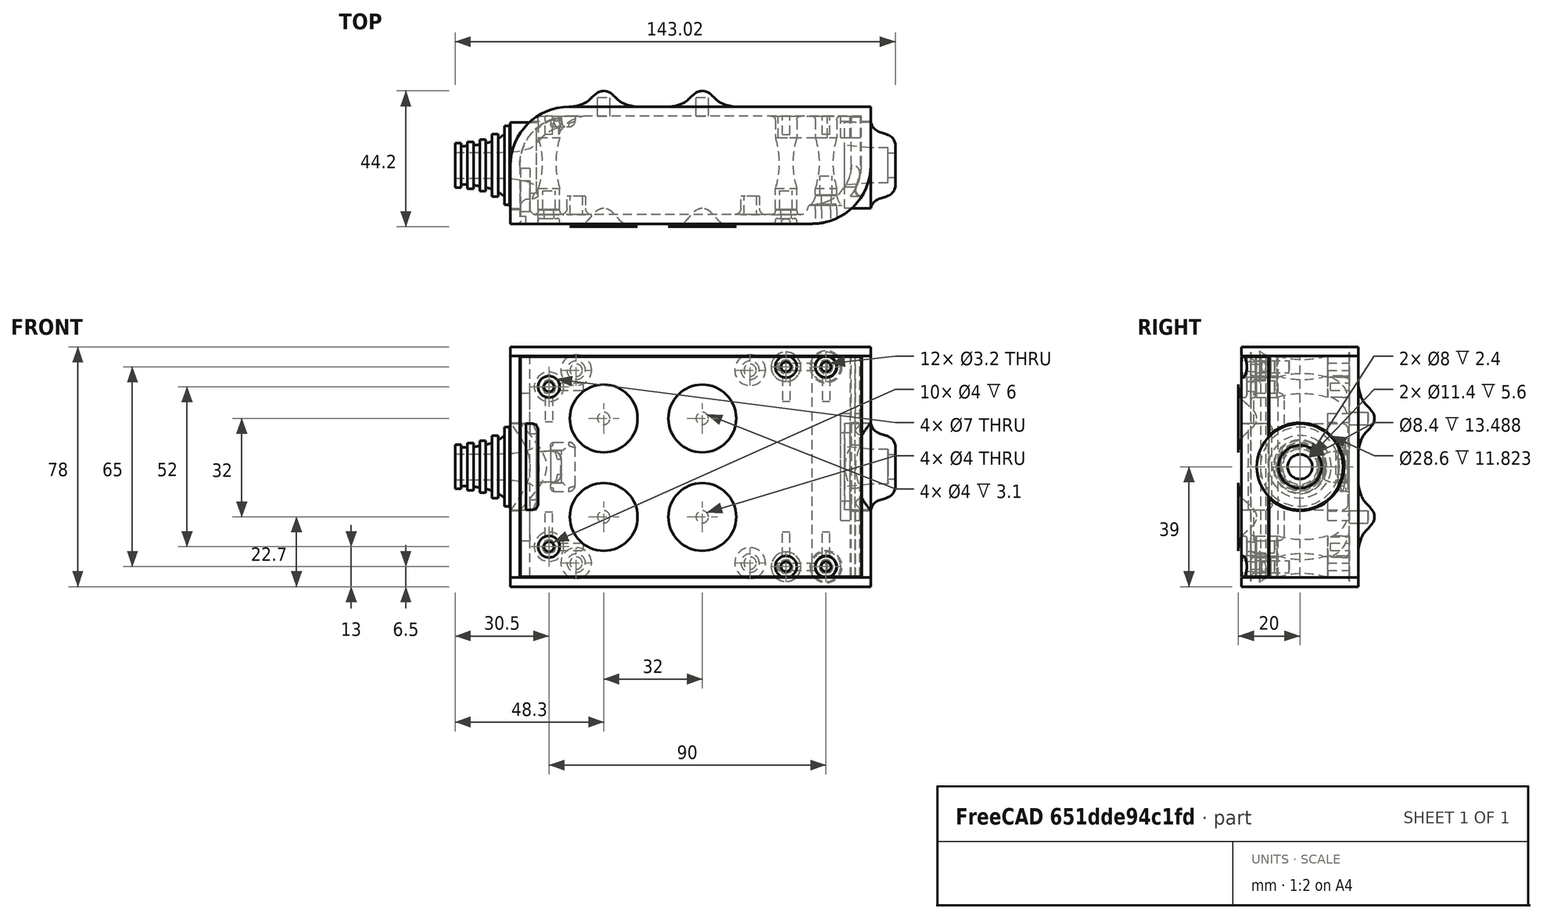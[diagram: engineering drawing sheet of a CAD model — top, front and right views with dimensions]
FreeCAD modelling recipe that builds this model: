
FCSTD DOCUMENT  (FreeCAD 0.19R0.19.2)
Label: enclosure_093
License: All rights reserved
LicenseURL: http://en.wikipedia.org/wiki/All_rights_reserved
objects: Part::Feature×72, Part::Revolution×72, Part::MultiFuse×52, Sketcher::SketchObject×29, Part::Fillet×22, Part::Cylinder×22, Part::Cut×19, Part::Extrusion×18, Part::Box×12, App::MeasureDistance×3
note: 318 computed .brp shape members not serialized (recipe doc carries the construction recipe); baked Part::Feature solids carry a one-line shape summary decoded from their .brp

FEATURE [Sketcher::SketchObject] Sketch  label="topSketch"
  FullyConstrained = true
  sketch-geometry (13):
    g0: LineSegment StartX=117 StartY=19 StartZ=0 EndX=117 EndY=38 EndZ=0
    g1: ArcOfCircle CenterX=98 CenterY=19 CenterZ=0 NormalX=0 NormalY=0 NormalZ=1 AngleXU=0 Radius=19 StartAngle=5.7297 EndAngle=6.28319
    g2: LineSegment StartX=0 StartY=3 StartZ=0 EndX=0 EndY=19 EndZ=0
    g3: LineSegment StartX=19 StartY=38 StartZ=0 EndX=117 EndY=38 EndZ=0
    g4: ArcOfCircle CenterX=19 CenterY=19 CenterZ=0 NormalX=0 NormalY=0 NormalZ=1 AngleXU=0 Radius=19 StartAngle=1.5708 EndAngle=3.14159
    g5: ArcOfCircle CenterX=19 CenterY=19 CenterZ=0 NormalX=0 NormalY=0 NormalZ=1 AngleXU=0 Radius=16 StartAngle=1.5708 EndAngle=3.14159
    g6: ArcOfCircle CenterX=98 CenterY=19 CenterZ=0 NormalX=0 NormalY=0 NormalZ=1 AngleXU=0 Radius=16 StartAngle=5.60905 EndAngle=6.28319
    g7: LineSegment StartX=114 StartY=19 StartZ=0 EndX=114 EndY=35 EndZ=0
    g8: LineSegment StartX=110.5 StartY=9.01251 StartZ=0 EndX=114.163 EndY=9.01251 EndZ=0
    g9: LineSegment StartX=114 StartY=35 StartZ=0 EndX=19 EndY=35 EndZ=0
    g10: LineSegment StartX=0 StartY=3 StartZ=0 EndX=0 EndY=0 EndZ=0
    g11: LineSegment StartX=3 StartY=0 StartZ=0 EndX=0 EndY=0 EndZ=0
    g12: LineSegment StartX=3 StartY=19 StartZ=0 EndX=3 EndY=0 EndZ=0
  constraints (33):
    c: Vertical(g0)
    c: Distance(g0) = 19
    c: Block(g0)
    c: Coincident(g1,g0)
    c: Block(g1)
    c: Vertical(g2)
    c: Block(g2)
    c: Coincident(g3,g0)
    c: Horizontal(g3)
    c: Distance(g3) = 98
    c: Coincident(g4,g3)
    c: Coincident(g4,g2)
    c: Block(g4)
    c: Coincident(g5,g4)
    c: Coincident(g6,g1)
    c: Block(g6)
    c: Block(g5)
    c: Coincident(g7,g6)
    c: Vertical(g7)
    c: Coincident(g8,g6)
    c: Coincident(g8,g1)
    c: Coincident(g9,g7)
    c: Coincident(g9,g5)
    c: Horizontal(g9)
    c: Tangent(g9,g5)
    c: Coincident(g10,g2)
    c: Distance(g10) = 3
    c: Vertical(g10)
    c: Coincident(g11,g10)
    c: Horizontal(g11)
    c: Coincident(g12,g5)
    c: Coincident(g12,g11)
    c: Vertical(g12)
FEATURE [Sketcher::SketchObject] Sketch001  label="bottomSketch"
  FullyConstrained = true
  sketch-geometry (32):
    g0: LineSegment StartX=3.3 StartY=-6.03275e-07 StartZ=0 EndX=98 EndY=-6.03275e-07 EndZ=0
    g1: ArcOfCircle CenterX=98 CenterY=19 CenterZ=0 NormalX=0 NormalY=0 NormalZ=1 AngleXU=0 Radius=19 StartAngle=4.71239 EndAngle=5.71103
    g2: LineSegment StartX=6.3 StartY=8 StartZ=0 EndX=3.3 EndY=8 EndZ=0
    g3: LineSegment StartX=3.3 StartY=8 StartZ=0 EndX=3.3 EndY=-6.03275e-07 EndZ=0
    g4: ArcOfCircle CenterX=8.3 CenterY=5 CenterZ=0 NormalX=0 NormalY=0 NormalZ=1 AngleXU=0 Radius=2 StartAngle=3.14159 EndAngle=4.71239
    g5: LineSegment StartX=6.3 StartY=8 StartZ=0 EndX=6.3 EndY=5 EndZ=0
    g6: ArcOfCircle CenterX=98 CenterY=19 CenterZ=0 NormalX=0 NormalY=0 NormalZ=1 AngleXU=0 Radius=12.7 StartAngle=4.71239 EndAngle=6.28319
    g7: LineSegment StartX=94.7 StartY=3 StartZ=0 EndX=8.3 EndY=3 EndZ=0
    g8-g12: Circle x5 (B-spline internal-alignment scaffolding for g13; pole/knot coordinates omitted)
    g13: BSplineCurve PolesCount=5 KnotsCount=3 Degree=3 IsPeriodic=0
    g14: GeomPoint X=98 Y=6.3 Z=0
    g15: GeomPoint X=96.3938 Y=4.71946 Z=0
    g16: GeomPoint X=94.7 Y=3 Z=0
    g17-g23: Circle x7 (B-spline internal-alignment scaffolding for g24; pole/knot coordinates omitted)
    g24: BSplineCurve PolesCount=7 KnotsCount=5 Degree=3 IsPeriodic=0
    g25-g29: GeomPoint x5 (B-spline internal-alignment scaffolding for g24; pole/knot coordinates omitted)
    g30: ArcOfCircle CenterX=98 CenterY=19 CenterZ=0 NormalX=0 NormalY=0 NormalZ=1 AngleXU=0 Radius=15.7 StartAngle=5.81226 EndAngle=6.28319
    g31: LineSegment StartX=110.7 StartY=19 StartZ=0 EndX=113.7 EndY=19 EndZ=0
  constraints (41):
    c: Horizontal(g0)
    c: Coincident(g1,g0)
    c: Block(g1)
    c: Horizontal(g2)
    c: Distance(g2) = 3
    c: Coincident(g3,g2)
    c: Vertical(g3)
    c: Coincident(g3,g0)
    c: Block(g4)
    c: Block(g2)
    c: Coincident(g5,g2)
    c: Coincident(g5,g4)
    c: Vertical(g5)
    c: Coincident(g6,g1)
    c: Block(g6)
    c: Coincident(g7,g4)
    c: Horizontal(g7)
    c: Block(g0)
    c: Block(g7)
    c: Block(g3)
    c: Coincident(g13,g6)
    c: Weight(g8) = 1
    c: Equal(g8, g9-g12) x4
    c: Coincident(g13,g7)
    c: InternalAlignment(g8-g12 -> g13) x5
    c: InternalAlignment(g14,g13)
    c: InternalAlignment(g15,g13)
    c: InternalAlignment(g16,g13)
    c: Block(g13)
    c: Weight(g17) = 1
    c: Equal(g17, g18-g23) x6
    c: Coincident(g24,g1)
    c: InternalAlignment(g17-g23 -> g24) x7
    c: InternalAlignment(g25-g29 -> g24) x5
    c: Block(g24)
    c: Coincident(g30,g24)
    c: Coincident(g31,g6)
    c: Coincident(g31,g30)
    c: Horizontal(g31)
    c: Block(g31)
    c: Block(g30)
FEATURE [Part::Extrusion] Extrude  label="top"
  Base = -> Sketch
  Dir = (0,0,1)
  DirMode = 2
  FaceMakerClass = Part::FaceMakerBullseye
  LengthFwd = 72
  LengthRev = 0
  Solid = true
  Symmetric = false
FEATURE [Part::Extrusion] Extrude001  label="bottom"
  Base = -> Sketch001
  Dir = (0,0,1)
  DirMode = 2
  FaceMakerClass = Part::FaceMakerBullseye
  LengthFwd = 71.4
  LengthRev = 0
  Placement = pos=(0,0,0.3) rot=(0,0,1;0rad)
  Solid = true
  Symmetric = false
FEATURE [Sketcher::SketchObject] Sketch002  label="topSketch001"
  FullyConstrained = true
  sketch-geometry (6):
    g0: LineSegment StartX=19 StartY=38 StartZ=0 EndX=117 EndY=38 EndZ=0
    g1: ArcOfCircle CenterX=19 CenterY=19 CenterZ=0 NormalX=0 NormalY=0 NormalZ=1 AngleXU=0 Radius=19 StartAngle=1.5708 EndAngle=3.14159
    g2: LineSegment StartX=117 StartY=38 StartZ=0 EndX=117 EndY=19 EndZ=0
    g3: LineSegment StartX=98 StartY=1.0161e-12 StartZ=0 EndX=5.22862e-06 EndY=1.0161e-12 EndZ=0
    g4: LineSegment StartX=5.22862e-06 StartY=19 StartZ=0 EndX=5.22862e-06 EndY=1.0161e-12 EndZ=0
    g5: ArcOfCircle CenterX=98 CenterY=19 CenterZ=0 NormalX=0 NormalY=0 NormalZ=1 AngleXU=0 Radius=19 StartAngle=4.71239 EndAngle=6.28319
  constraints (16):
    c: Horizontal(g0)
    c: Distance(g0) = 98
    c: Coincident(g1,g0)
    c: Block(g1)
    c: Coincident(g2,g0)
    c: Vertical(g2)
    c: Distance(g2) = 19
    c: Horizontal(g3)
    c: Coincident(g4,g1)
    c: Vertical(g4)
    c: Coincident(g3,g4)
    c: Block(g3)
    c: Coincident(g5,g2)
    c: Coincident(g5,g3)
    c: Block(g0)
    c: Block(g5)
FEATURE [Part::Extrusion] Extrude002  label="sideA"
  Base = -> Sketch002
  Dir = (0,0,1)
  DirMode = 2
  FaceMakerClass = Part::FaceMakerBullseye
  LengthFwd = 3
  LengthRev = 0
  Placement = pos=(0,0,-3) rot=(0,0,1;0rad)
  Solid = true
  Symmetric = false
FEATURE [Sketcher::SketchObject] Sketch003  label="topSketch002"
  FullyConstrained = true
  sketch-geometry (6):
    g0: LineSegment StartX=19 StartY=38 StartZ=0 EndX=117 EndY=38 EndZ=0
    g1: ArcOfCircle CenterX=19 CenterY=19 CenterZ=0 NormalX=0 NormalY=0 NormalZ=1 AngleXU=0 Radius=19 StartAngle=1.5708 EndAngle=3.14159
    g2: LineSegment StartX=117 StartY=38 StartZ=0 EndX=117 EndY=19 EndZ=0
    g3: LineSegment StartX=98 StartY=1.0161e-12 StartZ=0 EndX=5.22862e-06 EndY=1.0161e-12 EndZ=0
    g4: LineSegment StartX=5.22862e-06 StartY=19 StartZ=0 EndX=5.22862e-06 EndY=1.0161e-12 EndZ=0
    g5: ArcOfCircle CenterX=98 CenterY=19 CenterZ=0 NormalX=0 NormalY=0 NormalZ=1 AngleXU=0 Radius=19 StartAngle=4.71239 EndAngle=6.28319
  constraints (16):
    c: Horizontal(g0)
    c: Distance(g0) = 98
    c: Coincident(g1,g0)
    c: Block(g1)
    c: Coincident(g2,g0)
    c: Vertical(g2)
    c: Distance(g2) = 19
    c: Horizontal(g3)
    c: Coincident(g4,g1)
    c: Vertical(g4)
    c: Coincident(g3,g4)
    c: Block(g3)
    c: Coincident(g5,g2)
    c: Coincident(g5,g3)
    c: Block(g0)
    c: Block(g5)
FEATURE [Part::Extrusion] Extrude003  label="sideB"
  Base = -> Sketch003
  Dir = (0,0,1)
  DirMode = 2
  FaceMakerClass = Part::FaceMakerBullseye
  LengthFwd = 3
  LengthRev = 0
  Placement = pos=(0,0,72) rot=(0,0,1;0rad)
  Solid = true
  Symmetric = false
FEATURE [Sketcher::SketchObject] Sketch004
  FullyConstrained = true
  MapMode = 3
  Placement = pos=(0,0,0) rot=(1,0,0;1.5708rad)
  Support = -> [Extrude]
  sketch-geometry (8):
    g0: Circle CenterX=80.351 CenterY=-67.6202 CenterZ=0 NormalX=0 NormalY=0 NormalZ=1 AngleXU=0 Radius=2
    g1: Circle CenterX=80.351 CenterY=-67.6202 CenterZ=0 NormalX=0 NormalY=0 NormalZ=1 AngleXU=0 Radius=3
    g2: Circle CenterX=80.351 CenterY=-4.92017 CenterZ=0 NormalX=0 NormalY=0 NormalZ=1 AngleXU=0 Radius=2
    g3: Circle CenterX=80.351 CenterY=-4.92017 CenterZ=0 NormalX=0 NormalY=0 NormalZ=1 AngleXU=0 Radius=3
    g4: Circle CenterX=23.851 CenterY=-4.92017 CenterZ=0 NormalX=0 NormalY=0 NormalZ=1 AngleXU=0 Radius=2
    g5: Circle CenterX=23.851 CenterY=-4.92017 CenterZ=0 NormalX=0 NormalY=0 NormalZ=1 AngleXU=0 Radius=3
    g6: Circle CenterX=23.851 CenterY=-67.6202 CenterZ=0 NormalX=0 NormalY=0 NormalZ=1 AngleXU=0 Radius=2
    g7: Circle CenterX=23.851 CenterY=-67.6202 CenterZ=0 NormalX=0 NormalY=0 NormalZ=1 AngleXU=0 Radius=3
  constraints (8):
    c: Block(g3)
    c: Block(g2)
    c: Block(g1)
    c: Block(g0)
    c: Block(g6)
    c: Block(g7)
    c: Block(g4)
    c: Block(g5)
FEATURE [Part::Extrusion] Extrude004
  Base = -> Sketch004
  Dir = (0,-1,2e-16)
  DirMode = 2
  FaceMakerClass = Part::FaceMakerBullseye
  LengthFwd = 6
  LengthRev = 0
  Placement = pos=(0,9,0) rot=(0,0,1;0rad)
  Solid = true
  Symmetric = false
FEATURE [Sketcher::SketchObject] Sketch005
  FullyConstrained = true
  MapMode = 3
  Placement = pos=(0,0,0) rot=(1,0,0;1.5708rad)
  Support = -> [Extrude]
  sketch-geometry (8):
    g0: Circle CenterX=80.351 CenterY=-67.6202 CenterZ=0 NormalX=0 NormalY=0 NormalZ=1 AngleXU=0 Radius=3
    g1: Circle CenterX=80.351 CenterY=-4.92017 CenterZ=0 NormalX=0 NormalY=0 NormalZ=1 AngleXU=0 Radius=3
    g2: Circle CenterX=23.851 CenterY=-4.92017 CenterZ=0 NormalX=0 NormalY=0 NormalZ=1 AngleXU=0 Radius=3
    g3: Circle CenterX=23.851 CenterY=-67.6202 CenterZ=0 NormalX=0 NormalY=0 NormalZ=1 AngleXU=0 Radius=3
    g4: Circle CenterX=23.851 CenterY=-67.6202 CenterZ=0 NormalX=0 NormalY=0 NormalZ=1 AngleXU=0 Radius=5
    g5: Circle CenterX=80.351 CenterY=-67.6202 CenterZ=0 NormalX=0 NormalY=0 NormalZ=1 AngleXU=0 Radius=5
    g6: Circle CenterX=23.851 CenterY=-4.92017 CenterZ=0 NormalX=0 NormalY=0 NormalZ=1 AngleXU=0 Radius=5
    g7: Circle CenterX=80.351 CenterY=-4.92017 CenterZ=0 NormalX=0 NormalY=0 NormalZ=1 AngleXU=0 Radius=5
  constraints (8):
    c: Block(g1)
    c: Block(g0)
    c: Block(g3)
    c: Block(g2)
    c: Block(g5)
    c: Block(g4)
    c: Block(g6)
    c: Block(g7)
FEATURE [Part::Extrusion] Extrude005
  Base = -> Sketch005
  Dir = (0,-1,2e-16)
  DirMode = 2
  FaceMakerClass = Part::FaceMakerBullseye
  LengthFwd = 2
  LengthRev = 0
  Solid = true
  Symmetric = false
FEATURE [Sketcher::SketchObject] Sketch006
  FullyConstrained = true
  MapMode = 3
  Placement = pos=(0,0,0) rot=(1,0,0;1.5708rad)
  sketch-geometry (8):
    g0: Circle CenterX=80.351 CenterY=-67.6202 CenterZ=0 NormalX=0 NormalY=0 NormalZ=1 AngleXU=0 Radius=3
    g1: Circle CenterX=80.351 CenterY=-4.92017 CenterZ=0 NormalX=0 NormalY=0 NormalZ=1 AngleXU=0 Radius=3
    g2: Circle CenterX=23.851 CenterY=-4.92017 CenterZ=0 NormalX=0 NormalY=0 NormalZ=1 AngleXU=0 Radius=3
    g3: Circle CenterX=23.851 CenterY=-67.6202 CenterZ=0 NormalX=0 NormalY=0 NormalZ=1 AngleXU=0 Radius=3
    g4: Circle CenterX=23.851 CenterY=-67.6202 CenterZ=0 NormalX=0 NormalY=0 NormalZ=1 AngleXU=0 Radius=5
    g5: Circle CenterX=80.351 CenterY=-67.6202 CenterZ=0 NormalX=0 NormalY=0 NormalZ=1 AngleXU=0 Radius=5
    g6: Circle CenterX=23.851 CenterY=-4.92017 CenterZ=0 NormalX=0 NormalY=0 NormalZ=1 AngleXU=0 Radius=5
    g7: Circle CenterX=80.351 CenterY=-4.92017 CenterZ=0 NormalX=0 NormalY=0 NormalZ=1 AngleXU=0 Radius=5
  constraints (8):
    c: Block(g1)
    c: Block(g0)
    c: Block(g3)
    c: Block(g2)
    c: Block(g5)
    c: Block(g4)
    c: Block(g6)
    c: Block(g7)
FEATURE [Part::Extrusion] Extrude007
  Base = -> Sketch006
  Dir = (0,-1,2e-16)
  DirMode = 2
  FaceMakerClass = Part::FaceMakerBullseye
  LengthFwd = 2
  LengthRev = 0
  Solid = true
  Symmetric = false
FEATURE [Part::Fillet] Fillet
  Base = -> Extrude007
  Edges = 4 edges r=1.99: [Edge6,Edge12,Edge18,Edge24]
FEATURE [Part::Cut] Cut
  Base = -> Extrude005
  Placement = pos=(0,5,0) rot=(0,0,1;0rad)
  Tool = -> Fillet
FEATURE [Part::MultiFuse] Fusion  label="pCBScrews"
  Placement = pos=(-2.5,0,72.3) rot=(0,0,1;0rad)
  Shapes = -> [Extrude004,Cut]
FEATURE [App::MeasureDistance] Distance  label="Distance: 0.69 mm"
  Distance = 0.685967
  P1 = (24.0138,2.9647,0.3)
  P2 = (23.8901,3,-0.373787)
FEATURE [App::MeasureDistance] Distance001  label="Distance: 0.53 mm"
  Distance = 0.533607
  P1 = (80.2939,3,72.2334)
  P2 = (80.281,2.99661,71.7)
FEATURE [Part::Fillet] Fillet001
  Base = -> Extrude001
  Edges = 1 edges r=2.4: [Edge17]
FEATURE [Part::Fillet] Fillet002  label="bottom001"
  Base = -> Fillet001
  Edges = 1 edges r=2.4: [Edge36]
FEATURE [Part::Fillet] Fillet003  label="top001"
  Base = -> Extrude
  Edges = 1 edges r=2: [Edge1]
FEATURE [Sketcher::SketchObject] Sketch007
  FullyConstrained = true
  sketch-geometry (16):
    g0: LineSegment StartX=4 StartY=0 StartZ=0 EndX=4 EndY=2.4 EndZ=0
    g1: LineSegment StartX=4 StartY=2.4 StartZ=0 EndX=7 EndY=2.4 EndZ=0
    g2: LineSegment StartX=4 StartY=0 StartZ=0 EndX=5.7 EndY=0 EndZ=0
    g3: LineSegment StartX=5.7 StartY=0 StartZ=0 EndX=5.7 EndY=-5.6 EndZ=0
    g4-g8: Circle x5 (B-spline internal-alignment scaffolding for g9; pole/knot coordinates omitted)
    g9: BSplineCurve PolesCount=5 KnotsCount=3 Degree=3 IsPeriodic=0
    g10: GeomPoint X=7 Y=2.4 Z=0
    g11: GeomPoint X=10.4582 Y=-1.55472 Z=0
    g12: GeomPoint X=14 Y=-5.6 Z=0
    g13: LineSegment StartX=14 StartY=-5.6 StartZ=0 EndX=14 EndY=-14.1 EndZ=0
    g14: LineSegment StartX=14 StartY=-14.1 StartZ=0 EndX=6.5 EndY=-14.1 EndZ=0
    g15: LineSegment StartX=5.7 StartY=-5.6 StartZ=0 EndX=6.5 EndY=-14.1 EndZ=0
  constraints (28):
    c: Distance(g0) = 2.4
    c: Vertical(g0)
    c: Block(g0)
    c: Coincident(g1,g0)
    c: Horizontal(g1)
    c: Distance(g1) = 3
    c: Coincident(g2,g0)
    c: Horizontal(g2)
    c: Distance(g2) = 1.7
    c: Coincident(g3,g2)
    c: Vertical(g3)
    c: Distance(g3) = 5.6
    c: Coincident(g9,g1)
    c: Weight(g4) = 1
    c: Equal(g4, g5-g8) x4
    c: InternalAlignment(g4-g8 -> g9) x5
    c: InternalAlignment(g10,g9)
    c: InternalAlignment(g11,g9)
    c: InternalAlignment(g12,g9)
    c: Block(g9)
    c: Coincident(g13,g9)
    c: Vertical(g13)
    c: Distance(g13) = 8.5
    c: Coincident(g14,g13)
    c: Horizontal(g14)
    c: Distance(g14) = 7.5
    c: Coincident(g15,g3)
    c: Coincident(g15,g14)
FEATURE [Part::Feature] Face
  shape: bbox 10 x 16.5 x 2e-07 mm, 1 faces, 0 solids (baked)
FEATURE [Part::Revolution] Revolve  label="plugHousing"
  Angle = 360
  Axis = (0,1,0)
  Base = (0,0,0)
  FaceMakerClass = Part::FaceMakerBullseye
  Placement = pos=(0,0,36.15) rot=(0,0,1;0rad)
  Solid = false
  Source = -> Face
  Symmetric = false
FEATURE [Part::Feature] Face001
  shape: bbox 10 x 16.5 x 2e-07 mm, 1 faces, 0 solids (baked)
FEATURE [Part::Revolution] Revolve001  label="plugHousing001"
  Angle = 360
  Axis = (0,1,0)
  Base = (0,0,0)
  FaceMakerClass = Part::FaceMakerBullseye
  Placement = pos=(0,0,36.15) rot=(0,0,1;0rad)
  Solid = false
  Source = -> Face001
  Symmetric = false
FEATURE [Part::MultiFuse] Fusion001  label="plugHousing002"
  Placement = pos=(0,0,0) rot=(0,0,1;1.5708rad)
  Shapes = -> [Revolve001,Revolve]
FEATURE [Part::Feature] Face002
  shape: bbox 10 x 16.5 x 2e-07 mm, 1 faces, 0 solids (baked)
FEATURE [Part::Revolution] Revolve003  label="plugHousing005"
  Angle = 360
  Axis = (0,1,0)
  Base = (0,0,0)
  FaceMakerClass = Part::FaceMakerBullseye
  Placement = pos=(0,0,36.15) rot=(0,0,1;0rad)
  Solid = false
  Source = -> Face002
  Symmetric = false
FEATURE [Part::Feature] Face003
  shape: bbox 10 x 16.5 x 2e-07 mm, 1 faces, 0 solids (baked)
FEATURE [Part::Revolution] Revolve002  label="plugHousing003"
  Angle = 360
  Axis = (0,1,0)
  Base = (0,0,0)
  FaceMakerClass = Part::FaceMakerBullseye
  Placement = pos=(0,0,36.15) rot=(0,0,1;0rad)
  Solid = false
  Source = -> Face003
  Symmetric = false
FEATURE [Part::MultiFuse] Fusion002  label="plugHousing004"
  Placement = pos=(0,0,0) rot=(0,0,1;1.5708rad)
  Shapes = -> [Revolve002,Revolve003]
FEATURE [Part::MultiFuse] Fusion003  label="plugHousing006"
  Placement = pos=(0,19,0) rot=(0,0,1;3.14159rad)
  Shapes = -> [Fusion002,Fusion001]
FEATURE [Part::Feature] Face004
  shape: bbox 10 x 16.5 x 2e-07 mm, 1 faces, 0 solids (baked)
FEATURE [Part::Revolution] Revolve006  label="plugHousing010"
  Angle = 360
  Axis = (0,1,0)
  Base = (0,0,0)
  FaceMakerClass = Part::FaceMakerBullseye
  Placement = pos=(0,0,36.15) rot=(0,0,1;0rad)
  Solid = false
  Source = -> Face004
  Symmetric = false
FEATURE [Part::Feature] Face005
  shape: bbox 10 x 16.5 x 2e-07 mm, 1 faces, 0 solids (baked)
FEATURE [Part::Revolution] Revolve007  label="plugHousing011"
  Angle = 360
  Axis = (0,1,0)
  Base = (0,0,0)
  FaceMakerClass = Part::FaceMakerBullseye
  Placement = pos=(0,0,36.15) rot=(0,0,1;0rad)
  Solid = false
  Source = -> Face005
  Symmetric = false
FEATURE [Part::Feature] Face006
  shape: bbox 10 x 16.5 x 2e-07 mm, 1 faces, 0 solids (baked)
FEATURE [Part::Revolution] Revolve004  label="plugHousing007"
  Angle = 360
  Axis = (0,1,0)
  Base = (0,0,0)
  FaceMakerClass = Part::FaceMakerBullseye
  Placement = pos=(0,0,36.15) rot=(0,0,1;0rad)
  Solid = false
  Source = -> Face006
  Symmetric = false
FEATURE [Part::MultiFuse] Fusion004  label="plugHousing009"
  Placement = pos=(0,0,0) rot=(0,0,1;1.5708rad)
  Shapes = -> [Revolve004,Revolve007]
FEATURE [Part::Feature] Face007
  shape: bbox 10 x 16.5 x 2e-07 mm, 1 faces, 0 solids (baked)
FEATURE [Part::Revolution] Revolve005  label="plugHousing008"
  Angle = 360
  Axis = (0,1,0)
  Base = (0,0,0)
  FaceMakerClass = Part::FaceMakerBullseye
  Placement = pos=(0,0,36.15) rot=(0,0,1;0rad)
  Solid = false
  Source = -> Face007
  Symmetric = false
FEATURE [Part::MultiFuse] Fusion005  label="plugHousing012"
  Placement = pos=(0,0,0) rot=(0,0,1;1.5708rad)
  Shapes = -> [Revolve006,Revolve005]
FEATURE [Part::MultiFuse] Fusion006  label="plugHousing013"
  Placement = pos=(0,19,0) rot=(0,0,1;3.14159rad)
  Shapes = -> [Fusion005,Fusion004]
FEATURE [Part::MultiFuse] Fusion007  label="plugHousing014"
  Placement = pos=(122.621,0,-0.15) rot=(0,0,1;0rad)
  Shapes = -> [Fusion003,Fusion006]
FEATURE [Part::Cylinder] Cylinder002
  Angle = 360
  AttacherType = Attacher::AttachEngine3D
  Height = 20
  Placement = pos=(0,0,36.15) rot=(0,0,1;0rad)
  Radius = 4
FEATURE [Part::Cylinder] Cylinder003
  Angle = 360
  AttacherType = Attacher::AttachEngine3D
  Height = 10
  Placement = pos=(0,0,36.15) rot=(0,0,1;0rad)
  Radius = 4
FEATURE [Part::MultiFuse] Fusion009  label="removeToCreateHoleForPlugHousing"
  Placement = pos=(70,19,36.15) rot=(0,1,0;1.5708rad)
  Shapes = -> [Cylinder002,Cylinder003]
FEATURE [Part::Cylinder] Cylinder004
  Angle = 360
  AttacherType = Attacher::AttachEngine3D
  Height = 20
  Placement = pos=(0,0,36.15) rot=(0,0,1;0rad)
  Radius = 4
FEATURE [Part::Cylinder] Cylinder005
  Angle = 360
  AttacherType = Attacher::AttachEngine3D
  Height = 10
  Placement = pos=(0,0,36.15) rot=(0,0,1;0rad)
  Radius = 4
FEATURE [Part::MultiFuse] Fusion010  label="removeToCreateHoleForPlugHousing001"
  Placement = pos=(70,19,36.15) rot=(0,1,0;1.5708rad)
  Shapes = -> [Cylinder004,Cylinder005]
FEATURE [Part::Cut] Cut001
  Base = -> Fillet003
  Tool = -> Fusion010
FEATURE [Part::Cut] Cut002  label="Bottom"
  Base = -> Fillet002
  Tool = -> Fusion009
FEATURE [Part::Feature] Face008
  shape: bbox 10 x 16.5 x 2e-07 mm, 1 faces, 0 solids (baked)
FEATURE [Part::Revolution] Revolve011  label="plugHousing021"
  Angle = 360
  Axis = (0,1,0)
  Base = (0,0,0)
  FaceMakerClass = Part::FaceMakerBullseye
  Placement = pos=(0,0,36.15) rot=(0,0,1;0rad)
  Solid = false
  Source = -> Face008
  Symmetric = false
FEATURE [Part::Feature] Face009
  shape: bbox 10 x 16.5 x 2e-07 mm, 1 faces, 0 solids (baked)
FEATURE [Part::Revolution] Revolve012  label="plugHousing022"
  Angle = 360
  Axis = (0,1,0)
  Base = (0,0,0)
  FaceMakerClass = Part::FaceMakerBullseye
  Placement = pos=(0,0,36.15) rot=(0,0,1;0rad)
  Solid = false
  Source = -> Face009
  Symmetric = false
FEATURE [Part::Feature] Face010 .. Face013  x4 (patterned run collapsed; names and placements below)
  shape: bbox 10 x 16.5 x 2e-07 mm, 1 faces, 0 solids (baked)
FEATURE [Part::Revolution] Revolve015  label="plugHousing027"
  Angle = 360
  Axis = (0,1,0)
  Base = (0,0,0)
  FaceMakerClass = Part::FaceMakerBullseye
  Placement = pos=(0,0,36.15) rot=(0,0,1;0rad)
  Solid = false
  Source = -> Face013
  Symmetric = false
FEATURE [Part::Feature] Face014
  shape: bbox 10 x 16.5 x 2e-07 mm, 1 faces, 0 solids (baked)
FEATURE [Part::Feature] Face015
  shape: bbox 10 x 16.5 x 2e-07 mm, 1 faces, 0 solids (baked)
FEATURE [Part::Feature] Face016
  shape: bbox 10 x 16.5 x 2e-07 mm, 1 faces, 0 solids (baked)
FEATURE [Part::Revolution] Revolve019  label="plugHousing033"
  Angle = 360
  Axis = (0,1,0)
  Base = (0,0,0)
  FaceMakerClass = Part::FaceMakerBullseye
  Placement = pos=(0,0,36.15) rot=(0,0,1;0rad)
  Solid = false
  Source = -> Face016
  Symmetric = false
FEATURE [Part::Feature] Face017
  shape: bbox 10 x 16.5 x 2e-07 mm, 1 faces, 0 solids (baked)
FEATURE [Part::Revolution] Revolve020  label="plugHousing034"
  Angle = 360
  Axis = (0,1,0)
  Base = (0,0,0)
  FaceMakerClass = Part::FaceMakerBullseye
  Placement = pos=(0,0,36.15) rot=(0,0,1;0rad)
  Solid = false
  Source = -> Face017
  Symmetric = false
FEATURE [Part::Feature] Face018
  shape: bbox 10 x 16.5 x 2e-07 mm, 1 faces, 0 solids (baked)
FEATURE [Part::Revolution] Revolve016  label="plugHousing030"
  Angle = 360
  Axis = (0,1,0)
  Base = (0,0,0)
  FaceMakerClass = Part::FaceMakerBullseye
  Placement = pos=(0,0,36.15) rot=(0,0,1;0rad)
  Solid = false
  Source = -> Face018
  Symmetric = false
FEATURE [Part::MultiFuse] Fusion020  label="plugHousing038"
  Placement = pos=(0,0,0) rot=(0,0,1;1.5708rad)
  Shapes = -> [Revolve016,Revolve020]
FEATURE [Part::Feature] Face019
  shape: bbox 10 x 16.5 x 2e-07 mm, 1 faces, 0 solids (baked)
FEATURE [Part::Feature] Face020
  shape: bbox 10 x 16.5 x 2e-07 mm, 1 faces, 0 solids (baked)
FEATURE [Part::Revolution] Revolve017  label="plugHousing031"
  Angle = 360
  Axis = (0,1,0)
  Base = (0,0,0)
  FaceMakerClass = Part::FaceMakerBullseye
  Placement = pos=(0,0,36.15) rot=(0,0,1;0rad)
  Solid = false
  Source = -> Face020
  Symmetric = false
FEATURE [Part::MultiFuse] Fusion021  label="plugHousing039"
  Placement = pos=(0,0,0) rot=(0,0,1;1.5708rad)
  Shapes = -> [Revolve019,Revolve017]
FEATURE [Part::MultiFuse] Fusion023  label="plugHousing041"
  Placement = pos=(0,19,0) rot=(0,0,1;3.14159rad)
  Shapes = -> [Fusion021,Fusion020]
FEATURE [Part::Revolution] Revolve022  label="plugHousing043"
  Angle = 360
  Axis = (0,1,0)
  Base = (0,0,0)
  FaceMakerClass = Part::FaceMakerBullseye
  Placement = pos=(0,0,36.15) rot=(0,0,1;0rad)
  Solid = false
  Source = -> Face019
  Symmetric = false
FEATURE [Part::Feature] Face021
  shape: bbox 10 x 16.5 x 2e-07 mm, 1 faces, 0 solids (baked)
FEATURE [Part::Revolution] Revolve023  label="plugHousing044"
  Angle = 360
  Axis = (0,1,0)
  Base = (0,0,0)
  FaceMakerClass = Part::FaceMakerBullseye
  Placement = pos=(0,0,36.15) rot=(0,0,1;0rad)
  Solid = false
  Source = -> Face021
  Symmetric = false
FEATURE [Part::Feature] Face022
  shape: bbox 10 x 16.5 x 2e-07 mm, 1 faces, 0 solids (baked)
FEATURE [Part::Revolution] Revolve018  label="plugHousing032"
  Angle = 360
  Axis = (0,1,0)
  Base = (0,0,0)
  FaceMakerClass = Part::FaceMakerBullseye
  Placement = pos=(0,0,36.15) rot=(0,0,1;0rad)
  Solid = false
  Source = -> Face022
  Symmetric = false
FEATURE [Part::MultiFuse] Fusion022  label="plugHousing040"
  Placement = pos=(0,0,0) rot=(0,0,1;1.5708rad)
  Shapes = -> [Revolve018,Revolve023]
FEATURE [Part::Feature] Face023
  shape: bbox 10 x 16.5 x 2e-07 mm, 1 faces, 0 solids (baked)
FEATURE [Part::Revolution] Revolve021  label="plugHousing035"
  Angle = 360
  Axis = (0,1,0)
  Base = (0,0,0)
  FaceMakerClass = Part::FaceMakerBullseye
  Placement = pos=(0,0,36.15) rot=(0,0,1;0rad)
  Solid = false
  Source = -> Face023
  Symmetric = false
FEATURE [Part::MultiFuse] Fusion018  label="plugHousing036"
  Placement = pos=(0,0,0) rot=(0,0,1;1.5708rad)
  Shapes = -> [Revolve022,Revolve021]
FEATURE [Part::MultiFuse] Fusion019  label="plugHousing037"
  Placement = pos=(0,19,0) rot=(0,0,1;3.14159rad)
  Shapes = -> [Fusion018,Fusion022]
FEATURE [Part::MultiFuse] Fusion024  label="plugHousing042"
  Placement = pos=(122.621,0,-0.15) rot=(0,0,1;0rad)
  Shapes = -> [Fusion023,Fusion019]
FEATURE [Part::Cylinder] Cylinder006
  Angle = 360
  AttacherType = Attacher::AttachEngine3D
  Height = 20
  Placement = pos=(0,0,36.15) rot=(0,0,1;0rad)
  Radius = 14.3
FEATURE [Part::Cylinder] Cylinder007
  Angle = 360
  AttacherType = Attacher::AttachEngine3D
  Height = 10
  Placement = pos=(0,0,36.15) rot=(0,0,1;0rad)
  Radius = 4
FEATURE [Part::MultiFuse] Fusion026  label="removeToCreteHoleForPlugHousing"
  Placement = pos=(70,19,36) rot=(0,1,0;1.5708rad)
  Shapes = -> [Cylinder006,Cylinder007]
FEATURE [Part::Box] Box001  label="Cube001"
  AttacherType = Attacher::AttachEngine3D
  Height = 28
  Length = 3
  Placement = pos=(110.7,19,22) rot=(0,0,1;0rad)
  Width = 15.7
FEATURE [Part::Cut] Cut003  label="top002"
  Base = -> Cut001
  Tool = -> Fusion007
FEATURE [Part::Revolution] Revolve008  label="plugHousing015"
  Angle = 360
  Axis = (0,1,0)
  Base = (0,0,0)
  FaceMakerClass = Part::FaceMakerBullseye
  Placement = pos=(0,0,36.15) rot=(0,0,1;0rad)
  Solid = false
  Source = -> Face010
  Symmetric = false
FEATURE [Part::MultiFuse] Fusion013  label="plugHousing020"
  Placement = pos=(0,0,0) rot=(0,0,1;1.5708rad)
  Shapes = -> [Revolve008,Revolve012]
FEATURE [Part::Cut] Cut004  label="top003"
  Base = -> Cut003
  Placement = pos=(1,0,0) rot=(0,0,1;0rad)
  Tool = -> Fusion026
FEATURE [Part::Cylinder] Cylinder008
  Angle = 360
  AttacherType = Attacher::AttachEngine3D
  Height = 20
  Placement = pos=(0,0,36.15) rot=(0,0,1;0rad)
  Radius = 10.3
FEATURE [Part::Cylinder] Cylinder009
  Angle = 360
  AttacherType = Attacher::AttachEngine3D
  Height = 10
  Placement = pos=(0,0,36.15) rot=(0,0,1;0rad)
  Radius = 4
FEATURE [Part::MultiFuse] Fusion027  label="removeToCreteHoleForPlugHousing001"
  Placement = pos=(70,19,36) rot=(0,1,0;1.5708rad)
  Shapes = -> [Cylinder008,Cylinder009]
FEATURE [Part::Cut] Cut005  label="plugHousingTab"
  Base = -> Box001
  Tool = -> Fusion027
FEATURE [Part::MultiFuse] Fusion028  label="plugHousing045"
  Shapes = -> [Fusion024,Cut005]
FEATURE [Part::Box] Box002  label="Cube002"
  AttacherType = Attacher::AttachEngine3D
  Height = 28.8
  Length = 3
  Placement = pos=(107.3,28,21.6) rot=(0,0,1;0rad)
  Width = 7
FEATURE [Part::Box] Box003  label="Cube003"
  AttacherType = Attacher::AttachEngine3D
  Height = 3
  Length = 6.4
  Placement = pos=(107.3,28,18.6) rot=(0,0,1;0rad)
  Width = 7
FEATURE [Part::Box] Box004  label="Cube004"
  AttacherType = Attacher::AttachEngine3D
  Height = 3
  Length = 6.4
  Placement = pos=(107.3,28,50.4) rot=(0,0,1;0rad)
  Width = 7
FEATURE [Part::MultiFuse] Fusion029  label="plugHousingBracketHolder"
  Shapes = -> [Box004,Box002,Box003]
FEATURE [Part::Cylinder] Cylinder010
  Angle = 360
  AttacherType = Attacher::AttachEngine3D
  Height = 20
  Placement = pos=(0,0,36.15) rot=(0,0,1;0rad)
  Radius = 14.3
FEATURE [Part::Cylinder] Cylinder011
  Angle = 360
  AttacherType = Attacher::AttachEngine3D
  Height = 10
  Placement = pos=(0,0,36.15) rot=(0,0,1;0rad)
  Radius = 4
FEATURE [Part::MultiFuse] Fusion030  label="removeToCreteHoleForPlugHousing002"
  Placement = pos=(70,19,36) rot=(0,1,0;1.5708rad)
  Shapes = -> [Cylinder010,Cylinder011]
FEATURE [Part::Cut] Cut006  label="plugHousingBracketHolder001"
  Base = -> Fusion029
  Tool = -> Fusion030
FEATURE [Part::Cylinder] Cylinder012
  Angle = 360
  AttacherType = Attacher::AttachEngine3D
  Height = 20
  Placement = pos=(0,0,36.15) rot=(0,0,1;0rad)
  Radius = 7
FEATURE [Part::Cylinder] Cylinder013
  Angle = 360
  AttacherType = Attacher::AttachEngine3D
  Height = 10
  Placement = pos=(0,0,36.15) rot=(0,0,1;0rad)
  Radius = 4
FEATURE [Part::MultiFuse] Fusion032  label="removeToCreteHoleForPlugHousing003"
  Placement = pos=(70,19,36) rot=(0,1,0;1.5708rad)
  Shapes = -> [Cylinder012,Cylinder013]
FEATURE [Part::Cut] Cut007  label="bottom002"
  Base = -> Cut002
  Tool = -> Fusion032
FEATURE [Sketcher::SketchObject] Sketch008
  FullyConstrained = true
  sketch-geometry (54):
    g0: LineSegment StartX=-4.2 StartY=0 StartZ=0 EndX=-6.2 EndY=0 EndZ=0
    g1: LineSegment StartX=-14 StartY=-18 StartZ=0 EndX=-14 EndY=-26.5 EndZ=0
    g2: LineSegment StartX=-4.2 StartY=0 StartZ=0 EndX=-4.2 EndY=-13.4877 EndZ=0
    g3: Circle CenterX=-4.2 CenterY=-13.4877 CenterZ=0 NormalX=0 NormalY=0 NormalZ=1 AngleXU=0 Radius=1
    g4: Circle CenterX=-4.2 CenterY=-26.5 CenterZ=0 NormalX=0 NormalY=0 NormalZ=1 AngleXU=0 Radius=1
    g5: Circle CenterX=-8.2 CenterY=-26.5 CenterZ=0 NormalX=0 NormalY=0 NormalZ=1 AngleXU=0 Radius=1
    g6: BSplineCurve PolesCount=3 KnotsCount=2 Degree=2 IsPeriodic=0
    g7: GeomPoint X=-4.2 Y=-13.4877 Z=0
    g8: GeomPoint X=-8.2 Y=-26.5 Z=0
    g9: LineSegment StartX=-14 StartY=-26.5 StartZ=0 EndX=-8.2 EndY=-26.5 EndZ=0
    g10: LineSegment StartX=-10.15 StartY=-12 StartZ=0 EndX=-10.15 EndY=-14 EndZ=0
    g11: LineSegment StartX=-12.8401 StartY=-16 StartZ=0 EndX=-10.1571 EndY=-16 EndZ=0
    g12: LineSegment StartX=-10.15 StartY=-14 StartZ=0 EndX=-8.70761 EndY=-14 EndZ=0
    g13: LineSegment StartX=-12.8401 StartY=-16 StartZ=0 EndX=-12.8401 EndY=-17.6958 EndZ=0
    g14: LineSegment StartX=-10.15 StartY=-12 StartZ=0 EndX=-7.79258 EndY=-12 EndZ=0
    g15: Circle CenterX=-6.2215 CenterY=-2 CenterZ=0 NormalX=0 NormalY=0 NormalZ=1 AngleXU=0 Radius=1
    g16: Circle CenterX=-6.22762 CenterY=-2.58724 CenterZ=0 NormalX=0 NormalY=0 NormalZ=1 AngleXU=0 Radius=1
    g17: Circle CenterX=-6.32538 CenterY=-4 CenterZ=0 NormalX=0 NormalY=0 NormalZ=1 AngleXU=0 Radius=1
    g18: BSplineCurve PolesCount=3 KnotsCount=2 Degree=2 IsPeriodic=0
    g19: GeomPoint X=-6.2215 Y=-2 Z=0
    g20: GeomPoint X=-6.32538 Y=-4 Z=0
    g21: Circle CenterX=-6.48644 CenterY=-5.99526 CenterZ=0 NormalX=0 NormalY=0 NormalZ=1 AngleXU=0 Radius=1
    g22: Circle CenterX=-6.58486 CenterY=-6.99526 CenterZ=0 NormalX=0 NormalY=0 NormalZ=1 AngleXU=0 Radius=1
    g23: Circle CenterX=-6.77343 CenterY=-8 CenterZ=0 NormalX=0 NormalY=0 NormalZ=1 AngleXU=0 Radius=1
    g24: BSplineCurve PolesCount=3 KnotsCount=2 Degree=2 IsPeriodic=0
    g25: GeomPoint X=-6.48644 Y=-5.99526 Z=0
    g26: GeomPoint X=-6.77343 Y=-8 Z=0
    g27: Circle CenterX=-7.19003 CenterY=-10 CenterZ=0 NormalX=0 NormalY=0 NormalZ=1 AngleXU=0 Radius=1
    g28: Circle CenterX=-7.44407 CenterY=-11.0915 CenterZ=0 NormalX=0 NormalY=0 NormalZ=1 AngleXU=0 Radius=1
    g29: Circle CenterX=-7.79258 CenterY=-12 CenterZ=0 NormalX=0 NormalY=0 NormalZ=1 AngleXU=0 Radius=1
    g30: BSplineCurve PolesCount=3 KnotsCount=2 Degree=2 IsPeriodic=0
    g31: GeomPoint X=-7.19003 Y=-10 Z=0
    g32: GeomPoint X=-7.79258 Y=-12 Z=0
    g33: Circle CenterX=-8.70761 CenterY=-14 CenterZ=0 NormalX=0 NormalY=0 NormalZ=1 AngleXU=0 Radius=1
    g34: Circle CenterX=-9.33087 CenterY=-15.1837 CenterZ=0 NormalX=0 NormalY=0 NormalZ=1 AngleXU=0 Radius=1
    g35: Circle CenterX=-10.1571 CenterY=-16 CenterZ=0 NormalX=0 NormalY=0 NormalZ=1 AngleXU=0 Radius=1
    g36: BSplineCurve PolesCount=3 KnotsCount=2 Degree=2 IsPeriodic=0
    g37: GeomPoint X=-8.70761 Y=-14 Z=0
    g38: GeomPoint X=-10.1571 Y=-16 Z=0
    g39: Circle CenterX=-12.8401 CenterY=-17.6958 CenterZ=0 NormalX=0 NormalY=0 NormalZ=1 AngleXU=0 Radius=1
    g40: Circle CenterX=-13.3521 CenterY=-17.9027 CenterZ=0 NormalX=0 NormalY=0 NormalZ=1 AngleXU=0 Radius=1
    g41: Circle CenterX=-14 CenterY=-18 CenterZ=0 NormalX=0 NormalY=0 NormalZ=1 AngleXU=0 Radius=1
    g42: BSplineCurve PolesCount=3 KnotsCount=2 Degree=2 IsPeriodic=0
    g43: GeomPoint X=-12.8401 Y=-17.6958 Z=0
    g44: GeomPoint X=-14 Y=-18 Z=0
    g45: LineSegment StartX=-6.2 StartY=0 StartZ=0 EndX=-7.2 EndY=0 EndZ=0
    g46: LineSegment StartX=-7.2 StartY=0 StartZ=0 EndX=-7.2 EndY=-2 EndZ=0
    g47: LineSegment StartX=-7.2 StartY=-2 StartZ=0 EndX=-6.2215 EndY=-2 EndZ=0
    g48: LineSegment StartX=-6.32538 StartY=-4 StartZ=0 EndX=-7.65538 EndY=-4 EndZ=0
    g49: LineSegment StartX=-7.65538 StartY=-4 StartZ=0 EndX=-7.65538 EndY=-5.99526 EndZ=0
    g50: LineSegment StartX=-7.65538 StartY=-5.99526 StartZ=0 EndX=-6.48644 EndY=-5.99526 EndZ=0
    g51: LineSegment StartX=-6.77343 StartY=-8 StartZ=0 EndX=-8.43343 EndY=-8 EndZ=0
    g52: LineSegment StartX=-8.43343 StartY=-8 StartZ=0 EndX=-8.43343 EndY=-10 EndZ=0
    g53: LineSegment StartX=-8.43343 StartY=-10 StartZ=0 EndX=-7.19003 EndY=-10 EndZ=0
  constraints (112):
    c: Horizontal(g0)
    c: Distance(g0) = 2
    c: Block(g0)
    c: Vertical(g1)
    c: Coincident(g2,g0)
    c: Vertical(g2)
    c: Block(g2)
    c: Coincident(g6,g2)
    c: Weight(g3) = 1
    c: Equal(g3,g4)
    c: Equal(g3,g5)
    c: InternalAlignment(g3,g6)
    c: InternalAlignment(g4,g6)
    c: InternalAlignment(g5,g6)
    c: InternalAlignment(g7,g6)
    c: InternalAlignment(g8,g6)
    c: Block(g6)
    c: Coincident(g9,g1)
    c: Coincident(g9,g6)
    c: Horizontal(g9)
    c: Vertical(g10)
    c: Block(g10)
    c: Horizontal(g11)
    c: Block(g11)
    c: Coincident(g12,g10)
    c: Horizontal(g12)
    c: Block(g12)
    c: Coincident(g13,g11)
    c: Vertical(g13)
    c: Block(g13)
    c: Coincident(g14,g10)
    c: Horizontal(g14)
    c: Block(g14)
    c: Block(g9)
    c: Block(g1)
    c: Weight(g15) = 1
    c: Equal(g15,g16)
    c: Equal(g15,g17)
    c: InternalAlignment(g15,g18)
    c: InternalAlignment(g16,g18)
    c: InternalAlignment(g17,g18)
    c: InternalAlignment(g19,g18)
    c: InternalAlignment(g20,g18)
    c: Weight(g21) = 1
    c: Equal(g21,g22)
    c: Equal(g21,g23)
    c: InternalAlignment(g21,g24)
    c: InternalAlignment(g22,g24)
    c: InternalAlignment(g23,g24)
    c: InternalAlignment(g25,g24)
    c: InternalAlignment(g26,g24)
    c: Weight(g27) = 1
    c: Equal(g27,g28)
    c: Equal(g27,g29)
    c: Coincident(g30,g14)
    c: InternalAlignment(g27,g30)
    c: InternalAlignment(g28,g30)
    c: InternalAlignment(g29,g30)
    c: InternalAlignment(g31,g30)
    c: InternalAlignment(g32,g30)
    c: Coincident(g36,g12)
    c: Weight(g33) = 1
    c: Equal(g33,g34)
    c: Equal(g33,g35)
    c: Coincident(g36,g11)
    c: InternalAlignment(g33,g36)
    c: InternalAlignment(g34,g36)
    c: InternalAlignment(g35,g36)
    c: InternalAlignment(g37,g36)
    c: InternalAlignment(g38,g36)
    c: Coincident(g42,g13)
    c: Weight(g39) = 1
    c: Equal(g39,g40)
    c: Equal(g39,g41)
    c: Coincident(g42,g1)
    c: InternalAlignment(g39,g42)
    c: InternalAlignment(g40,g42)
    c: InternalAlignment(g41,g42)
    c: InternalAlignment(g43,g42)
    c: InternalAlignment(g44,g42)
    c: Block(g18)
    c: Block(g24)
    c: Block(g30)
    c: Block(g36)
    c: Block(g42)
    c: Horizontal(g45)
    c: Coincident(g45,g0)
    c: Vertical(g46)
    c: Coincident(g46,g45)
    c: Coincident(g47,g46)
    c: Coincident(g47,g18)
    c: Horizontal(g47)
    c: Block(g46)
    c: Coincident(g48,g18)
    c: Horizontal(g48)
    c: Distance(g48) = 1.33
    c: Vertical(g49)
    c: Coincident(g49,g48)
    c: Coincident(g50,g49)
    c: Coincident(g50,g24)
    c: Horizontal(g50)
    c: Tangent(g50,g22)
    c: Horizontal(g51)
    c: Coincident(g51,g24)
    c: Block(g51)
    c: Vertical(g52)
    c: Block(g52)
    c: Coincident(g52,g51)
    c: Coincident(g53,g52)
    c: Coincident(g53,g30)
    c: Horizontal(g53)
    c: Distance(g1) = 8.5
FEATURE [Part::Feature] Face024
  shape: bbox 9.8 x 26.5 x 2e-07 mm, 1 faces, 0 solids (baked)
FEATURE [Part::Revolution] Revolve024
  Angle = 360
  Axis = (0,1,0)
  Base = (0,0,0)
  FaceMakerClass = Part::FaceMakerBullseye
  Placement = pos=(0,0,0) rot=(0,0,1;1.5708rad)
  Solid = false
  Source = -> Face024
  Symmetric = false
FEATURE [Part::Feature] Face025
  shape: bbox 9.8 x 26.5 x 2e-07 mm, 1 faces, 0 solids (baked)
FEATURE [Part::Revolution] Revolve025
  Angle = 360
  Axis = (0,1,0)
  Base = (0,0,0)
  FaceMakerClass = Part::FaceMakerBullseye
  Placement = pos=(0,0,0) rot=(0,0,1;1.5708rad)
  Solid = false
  Source = -> Face025
  Symmetric = false
FEATURE [Part::MultiFuse] Fusion033
  Placement = pos=(-18,19,36) rot=(0,0,1;0rad)
  Shapes = -> [Revolve025,Revolve024]
FEATURE [Part::Cylinder] Cylinder014
  Angle = 360
  AttacherType = Attacher::AttachEngine3D
  Height = 20
  Placement = pos=(0,0,36.15) rot=(0,0,1;0rad)
  Radius = 14.3
FEATURE [Part::Cylinder] Cylinder015
  Angle = 360
  AttacherType = Attacher::AttachEngine3D
  Height = 10
  Placement = pos=(0,0,36.15) rot=(0,0,1;0rad)
  Radius = 4
FEATURE [Part::MultiFuse] Fusion034  label="removeToCreteHoleForPlugHousing004"
  Placement = pos=(-42,19,36) rot=(0,1,0;1.5708rad)
  Shapes = -> [Cylinder014,Cylinder015]
FEATURE [Part::Cut] Cut008  label="top004"
  Base = -> Cut004
  Placement = pos=(-1,0,0) rot=(0,0,1;0rad)
  Tool = -> Fusion034
FEATURE [Part::Box] Box005  label="Cube005"
  AttacherType = Attacher::AttachEngine3D
  Height = 28
  Length = 3
  Placement = pos=(110.7,19,22) rot=(0,0,1;0rad)
  Width = 15.7
FEATURE [Part::Cylinder] Cylinder016
  Angle = 360
  AttacherType = Attacher::AttachEngine3D
  Height = 10
  Placement = pos=(0,0,36.15) rot=(0,0,1;0rad)
  Radius = 4
FEATURE [Part::Cylinder] Cylinder017
  Angle = 360
  AttacherType = Attacher::AttachEngine3D
  Height = 20
  Placement = pos=(0,0,36.15) rot=(0,0,1;0rad)
  Radius = 10.3
FEATURE [Part::MultiFuse] Fusion035  label="removeToCreteHoleForPlugHousing005"
  Placement = pos=(70,19,36) rot=(0,1,0;1.5708rad)
  Shapes = -> [Cylinder017,Cylinder016]
FEATURE [Part::Cut] Cut009  label="plugHousingTab001"
  Base = -> Box005
  Placement = pos=(-107.4,-14,0) rot=(0,0,1;0rad)
  Tool = -> Fusion035
FEATURE [Part::Box] Box006  label="Cube006"
  AttacherType = Attacher::AttachEngine3D
  Height = 28
  Length = 3
  Placement = pos=(110.7,19,22) rot=(0,0,1;0rad)
  Width = 15.7
FEATURE [Part::Cylinder] Cylinder018
  Angle = 360
  AttacherType = Attacher::AttachEngine3D
  Height = 10
  Placement = pos=(0,0,36.15) rot=(0,0,1;0rad)
  Radius = 4
FEATURE [Part::Cylinder] Cylinder019
  Angle = 360
  AttacherType = Attacher::AttachEngine3D
  Height = 20
  Placement = pos=(0,0,36.15) rot=(0,0,1;0rad)
  Radius = 10.3
FEATURE [Part::MultiFuse] Fusion036  label="removeToCreteHoleForPlugHousing006"
  Placement = pos=(70,19,36) rot=(0,1,0;1.5708rad)
  Shapes = -> [Cylinder019,Cylinder018]
FEATURE [Part::Cut] Cut010  label="plugHousingTab002"
  Base = -> Box006
  Placement = pos=(-107.4,-14,0) rot=(0,0,1;0rad)
  Tool = -> Fusion036
FEATURE [Part::MultiFuse] Fusion037
  Placement = pos=(9.6,23,0) rot=(0,0,1;3.14159rad)
  Shapes = -> [Cut009,Cut010]
FEATURE [Part::Box] Box  label="Cube"
  AttacherType = Attacher::AttachEngine3D
  Height = 10
  Length = 3
  Placement = pos=(3.3,4,12) rot=(0,0,1;0rad)
  Width = 10
FEATURE [Part::Fillet] Fillet004
  Base = -> Fusion028
  Edges = 1 edges r=2: [Edge25]
FEATURE [Part::Fillet] Fillet005  label="plugHousing046"
  Base = -> Fillet004
  Edges = 1 edges r=2: [Edge8]
FEATURE [Part::Fillet] Fillet006
  Base = -> Box
  Edges = 1 edges r=2: [Edge11]
FEATURE [Part::Box] Box007  label="Cube007"
  AttacherType = Attacher::AttachEngine3D
  Height = 10
  Length = 3
  Placement = pos=(3.3,4,50) rot=(0,0,1;0rad)
  Width = 10
FEATURE [Part::Fillet] Fillet007
  Base = -> Box007
  Edges = 1 edges r=2: [Edge12]
FEATURE [Part::Box] Box008  label="Cube008"
  AttacherType = Attacher::AttachEngine3D
  Height = 28
  Length = 4
  Placement = pos=(5,0,22) rot=(0,0,1;0rad)
  Width = 10
FEATURE [Part::Fillet] Fillet008
  Base = -> Box008
  Edges = 1 edges r=1: [Edge7]
FEATURE [Part::Fillet] Fillet009
  Base = -> Fillet008
  Edges = 1 edges r=2: [Edge5]
FEATURE [Part::Fillet] Fillet010
  Base = -> Fillet009
  Edges = 1 edges r=2: [Edge2]
FEATURE [Sketcher::SketchObject] Sketch009  label="topSketch003"
  FullyConstrained = true
  sketch-geometry (4):
    g0: LineSegment StartX=16.8446 StartY=31.512 StartZ=0 EndX=16.3251 EndY=34.4666 EndZ=0
    g1: ArcOfCircle CenterX=19 CenterY=19.2524 CenterZ=0 NormalX=0 NormalY=0 NormalZ=1 AngleXU=0 Radius=15.4476 StartAngle=1.74483 EndAngle=2.72717
    g2: ArcOfCircle CenterX=19 CenterY=19.2524 CenterZ=0 NormalX=0 NormalY=0 NormalZ=1 AngleXU=0 Radius=12.4476 StartAngle=1.74483 EndAngle=2.73189
    g3: LineSegment StartX=4.86004 StartY=25.4725 StartZ=0 EndX=7.58253 EndY=24.2107 EndZ=0
  constraints (7):
    c: Block(g0)
    c: Coincident(g1,g0)
    c: Coincident(g2,g0)
    c: Coincident(g3,g1)
    c: Coincident(g3,g2)
    c: Block(g1)
    c: Block(g2)
FEATURE [Part::Extrusion] Extrude008
  Base = -> Sketch009
  Dir = (0,0,1)
  DirMode = 2
  FaceMakerClass = Part::FaceMakerBullseye
  LengthFwd = 10
  LengthRev = 0
  Placement = pos=(0,0,31) rot=(0,0,1;0rad)
  Solid = true
  Symmetric = false
FEATURE [Part::Cylinder] Cylinder020
  Angle = 360
  AttacherType = Attacher::AttachEngine3D
  Height = 20
  Placement = pos=(0,0,36.15) rot=(0,0,1;0rad)
  Radius = 8.2
FEATURE [Part::Cylinder] Cylinder021
  Angle = 360
  AttacherType = Attacher::AttachEngine3D
  Height = 10
  Placement = pos=(0,0,36.15) rot=(0,0,1;0rad)
  Radius = 4
FEATURE [Part::MultiFuse] Fusion038  label="removeToCreteHoleForPlugHousing007"
  Placement = pos=(-42,19,36) rot=(0,1,0;1.5708rad)
  Shapes = -> [Cylinder020,Cylinder021]
FEATURE [Part::Cut] Cut011
  Base = -> Extrude008
  Tool = -> Fusion038
FEATURE [Part::Fillet] Fillet011
  Base = -> Cut011
  Edges = 1 edges r=2: [Edge1]
FEATURE [Part::Fillet] Fillet012
  Base = -> Fillet011
  Edges = 1 edges r=2.5: [Edge1]
FEATURE [Part::Fillet] Fillet013
  Base = -> Fillet012
  Edges = 1 edges r=2.5: [Edge2]
FEATURE [Part::Box] Box010  label="Cube010"
  AttacherType = Attacher::AttachEngine3D
  Height = 16
  Length = 8
  Placement = pos=(12.7,31.52,28) rot=(0,0,1;0rad)
  Width = 4
FEATURE [Sketcher::SketchObject] Sketch010  label="topSketch004"
  FullyConstrained = true
  sketch-geometry (4):
    g0: LineSegment StartX=16.8446 StartY=31.512 StartZ=0 EndX=16.3251 EndY=34.4666 EndZ=0
    g1: ArcOfCircle CenterX=19 CenterY=19.2524 CenterZ=0 NormalX=0 NormalY=0 NormalZ=1 AngleXU=0 Radius=15.4476 StartAngle=1.74483 EndAngle=2.72717
    g2: ArcOfCircle CenterX=19 CenterY=19.2524 CenterZ=0 NormalX=0 NormalY=0 NormalZ=1 AngleXU=0 Radius=12.4476 StartAngle=1.74483 EndAngle=2.73189
    g3: LineSegment StartX=4.86004 StartY=25.4725 StartZ=0 EndX=7.58253 EndY=24.2107 EndZ=0
  constraints (7):
    c: Block(g0)
    c: Coincident(g1,g0)
    c: Coincident(g2,g0)
    c: Coincident(g3,g1)
    c: Coincident(g3,g2)
    c: Block(g1)
    c: Block(g2)
FEATURE [Part::Cylinder] Cylinder022
  Angle = 360
  AttacherType = Attacher::AttachEngine3D
  Height = 10
  Placement = pos=(0,0,36.15) rot=(0,0,1;0rad)
  Radius = 4
FEATURE [Sketcher::SketchObject] Sketch011  label="topSketch005"
  FullyConstrained = true
  sketch-geometry (4):
    g0: LineSegment StartX=16.8446 StartY=31.512 StartZ=0 EndX=16.3251 EndY=34.4666 EndZ=0
    g1: ArcOfCircle CenterX=19 CenterY=19.2524 CenterZ=0 NormalX=0 NormalY=0 NormalZ=1 AngleXU=0 Radius=15.4476 StartAngle=1.74483 EndAngle=2.72717
    g2: ArcOfCircle CenterX=19 CenterY=19.2524 CenterZ=0 NormalX=0 NormalY=0 NormalZ=1 AngleXU=0 Radius=12.4476 StartAngle=1.74483 EndAngle=2.73189
    g3: LineSegment StartX=4.86004 StartY=25.4725 StartZ=0 EndX=7.58253 EndY=24.2107 EndZ=0
  constraints (7):
    c: Block(g0)
    c: Coincident(g1,g0)
    c: Coincident(g2,g0)
    c: Coincident(g3,g1)
    c: Coincident(g3,g2)
    c: Block(g1)
    c: Block(g2)
FEATURE [Part::Extrusion] Extrude010
  Base = -> Sketch011
  Dir = (0,0,1)
  DirMode = 2
  FaceMakerClass = Part::FaceMakerBullseye
  LengthFwd = 10.6
  LengthRev = 0
  Placement = pos=(0,0,31) rot=(0,0,1;0rad)
  Solid = true
  Symmetric = false
FEATURE [Part::Cylinder] Cylinder023
  Angle = 360
  AttacherType = Attacher::AttachEngine3D
  Height = 20
  Placement = pos=(0,0,36.15) rot=(0,0,1;0rad)
  Radius = 8.2
FEATURE [Part::MultiFuse] Fusion039  label="removeToCreteHoleForPlugHousing008"
  Placement = pos=(-42,19,36) rot=(0,1,0;1.5708rad)
  Shapes = -> [Cylinder023,Cylinder022]
FEATURE [Part::Cut] Cut012
  Base = -> Extrude010
  Placement = pos=(0,0,-0.3) rot=(0,0,1;0rad)
  Tool = -> Fusion039
FEATURE [Part::Cut] Cut013
  Base = -> Box010
  Tool = -> Cut012
FEATURE [Part::Fillet] Fillet014
  Base = -> Cut013
  Edges = 1 edges r=0.7: [Edge13]
FEATURE [Part::Fillet] Fillet015
  Base = -> Fillet014
  Edges = 1 edges r=0.7: [Edge13]
FEATURE [Part::Fillet] Fillet016
  Base = -> Fillet015
  Edges = 1 edges r=0.7: [Edge16]
FEATURE [Part::Fillet] Fillet017
  Base = -> Fillet016
  Edges = 1 edges r=0.7: [Edge11]
FEATURE [Part::Fillet] Fillet018
  Base = -> Fillet017
  Edges = 1 edges r=0.7: [Edge10]
FEATURE [Part::Fillet] Fillet019
  Base = -> Fillet018
  Edges = 1 edges r=1.2: [Edge5]
FEATURE [Part::Fillet] Fillet020
  Base = -> Fillet019
  Edges = 1 edges r=1.2: [Edge12]
FEATURE [Part::Fillet] Fillet021
  Base = -> Fillet020
  Edges = 1 edges r=2: [Edge1]
  Placement = pos=(0.3,0,0) rot=(0,0,1;0rad)
FEATURE [Part::MultiFuse] Fusion040  label="top005"
  Shapes = -> [Cut008,Fillet021]
FEATURE [Part::MultiFuse] Fusion041  label="wireHolder"
  Shapes = -> [Fusion033,Fillet013]
FEATURE [Part::MultiFuse] Fusion042
  Shapes = -> [Fillet007,Fusion041]
FEATURE [Part::MultiFuse] Fusion043  label="wireHolder001"
  Shapes = -> [Fusion042,Fillet010]
FEATURE [Part::MultiFuse] Fusion044  label="wireHolder002"
  Shapes = -> [Fillet006,Fusion037,Fusion043]
FEATURE [Part::Feature] Face026
  shape: bbox 11 x 6 x 2e-07 mm, 1 faces, 0 solids (baked)
FEATURE [Part::Revolution] Revolve026
  Angle = 360
  Axis = (0,1,0)
  Base = (0,0,0)
  FaceMakerClass = Part::FaceMakerBullseye
  Placement = pos=(30.3,-1,19.7) rot=(0,0,1;0rad)
  Solid = false
  Source = -> Face026
  Symmetric = false
FEATURE [Sketcher::SketchObject] Sketch013  label="topSketch006"
  FullyConstrained = true
  sketch-geometry (13):
    g0: LineSegment StartX=117 StartY=19 StartZ=0 EndX=117 EndY=38 EndZ=0
    g1: ArcOfCircle CenterX=98 CenterY=19 CenterZ=0 NormalX=0 NormalY=0 NormalZ=1 AngleXU=0 Radius=19 StartAngle=5.7297 EndAngle=6.28319
    g2: LineSegment StartX=0 StartY=3 StartZ=0 EndX=0 EndY=19 EndZ=0
    g3: LineSegment StartX=19 StartY=38 StartZ=0 EndX=117 EndY=38 EndZ=0
    g4: ArcOfCircle CenterX=19 CenterY=19 CenterZ=0 NormalX=0 NormalY=0 NormalZ=1 AngleXU=0 Radius=19 StartAngle=1.5708 EndAngle=3.14159
    g5: ArcOfCircle CenterX=19 CenterY=19 CenterZ=0 NormalX=0 NormalY=0 NormalZ=1 AngleXU=0 Radius=16 StartAngle=1.5708 EndAngle=3.14159
    g6: ArcOfCircle CenterX=98 CenterY=19 CenterZ=0 NormalX=0 NormalY=0 NormalZ=1 AngleXU=0 Radius=16 StartAngle=5.60905 EndAngle=6.28319
    g7: LineSegment StartX=114 StartY=19 StartZ=0 EndX=114 EndY=35 EndZ=0
    g8: LineSegment StartX=110.5 StartY=9.01251 StartZ=0 EndX=114.163 EndY=9.01251 EndZ=0
    g9: LineSegment StartX=114 StartY=35 StartZ=0 EndX=19 EndY=35 EndZ=0
    g10: LineSegment StartX=0 StartY=3 StartZ=0 EndX=0 EndY=0 EndZ=0
    g11: LineSegment StartX=3 StartY=0 StartZ=0 EndX=0 EndY=0 EndZ=0
    g12: LineSegment StartX=3 StartY=19 StartZ=0 EndX=3 EndY=0 EndZ=0
  constraints (33):
    c: Vertical(g0)
    c: Distance(g0) = 19
    c: Block(g0)
    c: Coincident(g1,g0)
    c: Block(g1)
    c: Vertical(g2)
    c: Block(g2)
    c: Coincident(g3,g0)
    c: Horizontal(g3)
    c: Distance(g3) = 98
    c: Coincident(g4,g3)
    c: Coincident(g4,g2)
    c: Block(g4)
    c: Coincident(g5,g4)
    c: Coincident(g6,g1)
    c: Block(g6)
    c: Block(g5)
    c: Coincident(g7,g6)
    c: Vertical(g7)
    c: Coincident(g8,g6)
    c: Coincident(g8,g1)
    c: Coincident(g9,g7)
    c: Coincident(g9,g5)
    c: Horizontal(g9)
    c: Tangent(g9,g5)
    c: Coincident(g10,g2)
    c: Distance(g10) = 3
    c: Vertical(g10)
    c: Coincident(g11,g10)
    c: Horizontal(g11)
    c: Coincident(g12,g5)
    c: Coincident(g12,g11)
    c: Vertical(g12)
FEATURE [Part::Extrusion] Extrude011  label="top006"
  Base = -> Sketch013
  Dir = (0,0,1)
  DirMode = 2
  FaceMakerClass = Part::FaceMakerBullseye
  LengthFwd = 72
  LengthRev = 0
  Solid = true
  Symmetric = false
FEATURE [Sketcher::SketchObject] Sketch014
  FullyConstrained = true
  MapMode = 3
  Placement = pos=(0,0,0) rot=(1,0,0;1.5708rad)
  Support = -> [Extrude011]
  sketch-geometry (8):
    g0: Circle CenterX=80.351 CenterY=-67.6202 CenterZ=0 NormalX=0 NormalY=0 NormalZ=1 AngleXU=0 Radius=2
    g1: Circle CenterX=80.351 CenterY=-67.6202 CenterZ=0 NormalX=0 NormalY=0 NormalZ=1 AngleXU=0 Radius=3
    g2: Circle CenterX=80.351 CenterY=-4.92017 CenterZ=0 NormalX=0 NormalY=0 NormalZ=1 AngleXU=0 Radius=2
    g3: Circle CenterX=80.351 CenterY=-4.92017 CenterZ=0 NormalX=0 NormalY=0 NormalZ=1 AngleXU=0 Radius=3
    g4: Circle CenterX=23.851 CenterY=-4.92017 CenterZ=0 NormalX=0 NormalY=0 NormalZ=1 AngleXU=0 Radius=2
    g5: Circle CenterX=23.851 CenterY=-4.92017 CenterZ=0 NormalX=0 NormalY=0 NormalZ=1 AngleXU=0 Radius=3
    g6: Circle CenterX=23.851 CenterY=-67.6202 CenterZ=0 NormalX=0 NormalY=0 NormalZ=1 AngleXU=0 Radius=2
    g7: Circle CenterX=23.851 CenterY=-67.6202 CenterZ=0 NormalX=0 NormalY=0 NormalZ=1 AngleXU=0 Radius=3
  constraints (8):
    c: Block(g3)
    c: Block(g2)
    c: Block(g1)
    c: Block(g0)
    c: Block(g6)
    c: Block(g7)
    c: Block(g4)
    c: Block(g5)
FEATURE [Part::Feature] Face027
  shape: bbox 11 x 6 x 2e-07 mm, 1 faces, 0 solids (baked)
FEATURE [Part::Revolution] Revolve027
  Angle = 360
  Axis = (0,1,0)
  Base = (0,0,0)
  FaceMakerClass = Part::FaceMakerBullseye
  Placement = pos=(30.3,-1,51.7) rot=(0,0,1;0rad)
  Solid = false
  Source = -> Face027
  Symmetric = false
FEATURE [Part::Feature] Face028
  shape: bbox 11 x 6 x 2e-07 mm, 1 faces, 0 solids (baked)
FEATURE [Part::Revolution] Revolve028
  Angle = 360
  Axis = (0,1,0)
  Base = (0,0,0)
  FaceMakerClass = Part::FaceMakerBullseye
  Placement = pos=(62.3,-1,19.7) rot=(0,0,1;0rad)
  Solid = false
  Source = -> Face028
  Symmetric = false
FEATURE [Part::Feature] Face029
  shape: bbox 11 x 6 x 2e-07 mm, 1 faces, 0 solids (baked)
FEATURE [Part::Revolution] Revolve029
  Angle = 360
  Axis = (0,1,0)
  Base = (0,0,0)
  FaceMakerClass = Part::FaceMakerBullseye
  Placement = pos=(62.3,-1,51.7) rot=(0,0,1;0rad)
  Solid = false
  Source = -> Face029
  Symmetric = false
FEATURE [Part::Feature] Wire
  shape: bbox 11 x 5.2 x 2e-07 mm, 0 faces, 0 solids (baked)
FEATURE [Part::Revolution] Revolve030
  Angle = 360
  Axis = (0,1,0)
  Base = (0,0,0)
  FaceMakerClass = Part::FaceMakerBullseye
  Placement = pos=(30.3,38,19.7) rot=(0,0,1;0rad)
  Solid = true
  Source = -> Wire
  Symmetric = false
FEATURE [Part::Feature] Wire001
  shape: bbox 11 x 5.2 x 2e-07 mm, 0 faces, 0 solids (baked)
FEATURE [Part::Revolution] Revolve031
  Angle = 360
  Axis = (0,1,0)
  Base = (0,0,0)
  FaceMakerClass = Part::FaceMakerBullseye
  Placement = pos=(30.3,38,51.7) rot=(0,0,1;0rad)
  Solid = true
  Source = -> Wire001
  Symmetric = false
FEATURE [Part::Feature] Wire002
  shape: bbox 11 x 5.2 x 2e-07 mm, 0 faces, 0 solids (baked)
FEATURE [Part::Revolution] Revolve032
  Angle = 360
  Axis = (0,1,0)
  Base = (0,0,0)
  FaceMakerClass = Part::FaceMakerBullseye
  Placement = pos=(62.3,38,51.7) rot=(0,0,1;0rad)
  Solid = true
  Source = -> Wire002
  Symmetric = false
FEATURE [Part::Feature] Wire003
  shape: bbox 11 x 5.2 x 2e-07 mm, 0 faces, 0 solids (baked)
FEATURE [Part::Revolution] Revolve033
  Angle = 360
  Axis = (0,1,0)
  Base = (0,0,0)
  FaceMakerClass = Part::FaceMakerBullseye
  Placement = pos=(62.3,38,19.7) rot=(0,0,1;0rad)
  Solid = true
  Source = -> Wire003
  Symmetric = false
FEATURE [Part::MultiFuse] Fusion045  label="altRandScrewHousing"
  Shapes = -> [Revolve029,Revolve027,Revolve028,Revolve026]
FEATURE [Part::MultiFuse] Fusion046  label="fanScrewHousing"
  Shapes = -> [Revolve033,Revolve032,Revolve031,Revolve030]
FEATURE [Sketcher::SketchObject] Sketch015
  FullyConstrained = true
  sketch-geometry (17):
    g0: Circle CenterX=-3.5 CenterY=23.5 CenterZ=0 NormalX=0 NormalY=0 NormalZ=1 AngleXU=0 Radius=1
    g1: Circle CenterX=-1 CenterY=15.25 CenterZ=0 NormalX=0 NormalY=0 NormalZ=1 AngleXU=0 Radius=1
    g2: Circle CenterX=-3.5 CenterY=7 CenterZ=0 NormalX=0 NormalY=0 NormalZ=1 AngleXU=0 Radius=1
    g3: BSplineCurve PolesCount=3 KnotsCount=2 Degree=2 IsPeriodic=0
    g4: GeomPoint X=-3.5 Y=23.5 Z=0
    g5: GeomPoint X=-3.5 Y=7 Z=0
    g6: Circle CenterX=-4.8 CenterY=30.5 CenterZ=0 NormalX=0 NormalY=0 NormalZ=1 AngleXU=0 Radius=1
    g7: Circle CenterX=-3.5 CenterY=30.5 CenterZ=0 NormalX=0 NormalY=0 NormalZ=1 AngleXU=0 Radius=1
    g8: Circle CenterX=-3.5 CenterY=29.2 CenterZ=0 NormalX=0 NormalY=0 NormalZ=1 AngleXU=0 Radius=1
    g9: BSplineCurve PolesCount=3 KnotsCount=2 Degree=2 IsPeriodic=0
    g10: GeomPoint X=-4.8 Y=30.5 Z=0
    g11: GeomPoint X=-3.5 Y=29.2 Z=0
    g12: LineSegment StartX=-3.5 StartY=29.2 StartZ=0 EndX=-3.5 EndY=23.5 EndZ=0
    g13: LineSegment StartX=-4.8 StartY=30.5 StartZ=0 EndX=0 EndY=30.5 EndZ=0
    g14: LineSegment StartX=-3.5 StartY=0.3 StartZ=0 EndX=0 EndY=0.3 EndZ=0
    g15: LineSegment StartX=-3.5 StartY=0.3 StartZ=0 EndX=-3.5 EndY=7 EndZ=0
    g16: LineSegment StartX=0 StartY=0.3 StartZ=0 EndX=0 EndY=30.5 EndZ=0
  constraints (33):
    c: Weight(g0) = 1
    c: Equal(g0,g1)
    c: Equal(g0,g2)
    c: InternalAlignment(g0,g3)
    c: InternalAlignment(g1,g3)
    c: InternalAlignment(g2,g3)
    c: InternalAlignment(g4,g3)
    c: InternalAlignment(g5,g3)
    c: Block(g3)
    c: Weight(g6) = 1
    c: Equal(g6,g7)
    c: Equal(g6,g8)
    c: InternalAlignment(g6,g9)
    c: InternalAlignment(g7,g9)
    c: InternalAlignment(g8,g9)
    c: InternalAlignment(g10,g9)
    c: InternalAlignment(g11,g9)
    c: Block(g9)
    c: Coincident(g12,g9)
    c: Coincident(g12,g3)
    c: Vertical(g12)
    c: Coincident(g13,g9)
    c: Horizontal(g13)
    c: Distance(g13) = 4.8
    c: Horizontal(g14)
    c: Block(g14)
    c: Coincident(g15,g14)
    c: Coincident(g15,g3)
    c: Vertical(g15)
    c: Coincident(g16,g14)
    c: Coincident(g16,g13)
    c: Vertical(g16)
    c: Tangent(g16,g1)
FEATURE [Sketcher::SketchObject] Sketch016
  FullyConstrained = true
  sketch-geometry (16):
    g0: Circle CenterX=-3.5 CenterY=23.5 CenterZ=0 NormalX=0 NormalY=0 NormalZ=1 AngleXU=0 Radius=1
    g1: Circle CenterX=-1 CenterY=15.25 CenterZ=0 NormalX=0 NormalY=0 NormalZ=1 AngleXU=0 Radius=1
    g2: Circle CenterX=-3.5 CenterY=7 CenterZ=0 NormalX=0 NormalY=0 NormalZ=1 AngleXU=0 Radius=1
    g3: BSplineCurve PolesCount=3 KnotsCount=2 Degree=2 IsPeriodic=0
    g4: GeomPoint X=-3.5 Y=23.5 Z=0
    g5: GeomPoint X=-3.5 Y=7 Z=0
    g6: LineSegment StartX=-3.5 StartY=28.2 StartZ=0 EndX=-3.5 EndY=23.5 EndZ=0
    g7: LineSegment StartX=0 StartY=29.5 StartZ=0 EndX=0 EndY=30 EndZ=0
    g8: LineSegment StartX=-3.5 StartY=28.2 StartZ=0 EndX=-3.5 EndY=30 EndZ=0
    g9: LineSegment StartX=0 StartY=30 StartZ=0 EndX=0 EndY=30.5 EndZ=0
    g10: LineSegment StartX=0 StartY=30.5 StartZ=0 EndX=-3.5 EndY=30.5 EndZ=0
    g11: LineSegment StartX=-3.5 StartY=30.5 StartZ=0 EndX=-3.5 EndY=30 EndZ=0
    g12: LineSegment StartX=0 StartY=29.5 StartZ=0 EndX=0 EndY=5 EndZ=0
    g13: LineSegment StartX=-3.5 StartY=0.3 StartZ=0 EndX=-3.5 EndY=7 EndZ=0
    g14: LineSegment StartX=-3.5 StartY=0.3 StartZ=0 EndX=0 EndY=0.3 EndZ=0
    g15: LineSegment StartX=0 StartY=5 StartZ=0 EndX=0 EndY=0.3 EndZ=0
  constraints (39):
    c: Weight(g0) = 1
    c: Equal(g0,g1)
    c: Equal(g0,g2)
    c: InternalAlignment(g0,g3)
    c: InternalAlignment(g1,g3)
    c: InternalAlignment(g2,g3)
    c: InternalAlignment(g4,g3)
    c: InternalAlignment(g5,g3)
    c: Block(g3)
    c: Coincident(g6,g3)
    c: Vertical(g6)
    c: Vertical(g7)
    c: Distance(g7) = 0.5
    c: Coincident(g8,g6)
    c: Vertical(g8)
    c: Block(g6)
    c: Block(g7)
    c: Vertical(g9)
    c: Equal(g7,g9) = 0.5
    c: Block(g9)
    c: Coincident(g9,g7)
    c: Horizontal(g10)
    c: Coincident(g10,g9)
    c: Coincident(g11,g10)
    c: Coincident(g11,g8)
    c: Vertical(g11)
    c: Block(g11)
    c: Coincident(g12,g7)
    c: Vertical(g12)
    c: Coincident(g13,g3)
    c: Vertical(g13)
    c: Distance(g13) = 6.7
    c: Coincident(g14,g13)
    c: Horizontal(g14)
    c: Block(g14)
    c: Coincident(g15,g12)
    c: Coincident(g15,g14)
    c: Vertical(g15)
    c: Block(g15)
FEATURE [Sketcher::SketchObject] Sketch017
  FullyConstrained = true
  sketch-geometry (11):
    g0: LineSegment StartX=-3.5 StartY=1e-16 StartZ=0 EndX=-1.6 EndY=1e-16 EndZ=0
    g1: LineSegment StartX=-1.6 StartY=1e-16 StartZ=0 EndX=-1.6 EndY=1.5 EndZ=0
    g2: LineSegment StartX=-3.5 StartY=1.5 StartZ=0 EndX=-1.6 EndY=1.5 EndZ=0
    g3: LineSegment StartX=-3.5 StartY=1e-16 StartZ=0 EndX=-4.8 EndY=1e-16 EndZ=0
    g4: Circle CenterX=-3.5 CenterY=1.3 CenterZ=0 NormalX=0 NormalY=0 NormalZ=1 AngleXU=0 Radius=1
    g5: Circle CenterX=-3.5 CenterY=1e-16 CenterZ=0 NormalX=0 NormalY=0 NormalZ=1 AngleXU=0 Radius=1
    g6: Circle CenterX=-4.8 CenterY=1e-16 CenterZ=0 NormalX=0 NormalY=0 NormalZ=1 AngleXU=0 Radius=1
    g7: BSplineCurve PolesCount=3 KnotsCount=2 Degree=2 IsPeriodic=0
    g8: GeomPoint X=-3.5 Y=1.3 Z=0
    g9: GeomPoint X=-4.8 Y=1e-16 Z=0
    g10: LineSegment StartX=-3.5 StartY=1.3 StartZ=0 EndX=-3.5 EndY=1.5 EndZ=0
  constraints (24):
    c: Horizontal(g0)
    c: Distance(g0) = 1.9
    c: Block(g0)
    c: Coincident(g1,g0)
    c: Vertical(g1)
    c: Coincident(g2,g1)
    c: Horizontal(g2)
    c: Coincident(g3,g0)
    c: Horizontal(g3)
    c: Distance(g3) = 1.3
    c: Weight(g4) = 1
    c: Equal(g4,g5)
    c: Coincident(g5,g0)
    c: Equal(g4,g6)
    c: Coincident(g7,g3)
    c: InternalAlignment(g4,g7)
    c: InternalAlignment(g5,g7)
    c: InternalAlignment(g6,g7)
    c: InternalAlignment(g8,g7)
    c: InternalAlignment(g9,g7)
    c: Coincident(g10,g7)
    c: Coincident(g10,g2)
    c: Vertical(g10)
    c: Block(g10)
FEATURE [Part::Feature] Face035
  shape: bbox 3.2 x 1.5 x 2e-07 mm, 1 faces, 0 solids (baked)
FEATURE [Part::Revolution] Revolve039  label="backCaseScrewRetainer"
  Angle = 360
  Axis = (0,1,0)
  Base = (0,0,0)
  FaceMakerClass = Part::FaceMakerBullseye
  Placement = pos=(12.5,3,62) rot=(0,0,1;0rad)
  Solid = false
  Source = -> Face035
  Symmetric = false
FEATURE [Part::Feature] Face036
  shape: bbox 3.2 x 1.5 x 2e-07 mm, 1 faces, 0 solids (baked)
FEATURE [Part::Feature] Face039
  shape: bbox 4.8 x 30.2 x 2e-07 mm, 1 faces, 0 solids (baked)
FEATURE [Part::Revolution] Revolve043  label="frontCaseScrewPost002"
  Angle = 360
  Axis = (0,1,0)
  Base = (0,0,0)
  FaceMakerClass = Part::FaceMakerBullseye
  Placement = pos=(89.5,4.5,3.5) rot=(0,0,1;0rad)
  Solid = false
  Source = -> Face039
  Symmetric = false
FEATURE [Part::Feature] Face042
  shape: bbox 4.8 x 30.2 x 2e-07 mm, 1 faces, 0 solids (baked)
FEATURE [Part::Revolution] Revolve046  label="frontCaseScrewPost003"
  Angle = 360
  Axis = (0,1,0)
  Base = (0,0,0)
  FaceMakerClass = Part::FaceMakerBullseye
  Placement = pos=(89.5,4.5,68.5) rot=(0,0,1;0rad)
  Solid = false
  Source = -> Face042
  Symmetric = false
FEATURE [Part::Feature] Face043
  shape: bbox 3.2 x 1.5 x 2e-07 mm, 1 faces, 0 solids (baked)
FEATURE [Part::Revolution] Revolve047  label="frontCaseScrewRetainer002"
  Angle = 360
  Axis = (0,1,0)
  Base = (0,0,0)
  FaceMakerClass = Part::FaceMakerBullseye
  Placement = pos=(89.5,3,68.5) rot=(0,0,1;0rad)
  Solid = false
  Source = -> Face043
  Symmetric = false
FEATURE [Part::Feature] Face044
  shape: bbox 3.2 x 1.5 x 2e-07 mm, 1 faces, 0 solids (baked)
FEATURE [Part::Revolution] Revolve048  label="frontCaseScrewRetainer003"
  Angle = 360
  Axis = (0,1,0)
  Base = (0,0,0)
  FaceMakerClass = Part::FaceMakerBullseye
  Placement = pos=(89.5,3,3.5) rot=(0,0,1;0rad)
  Solid = false
  Source = -> Face044
  Symmetric = false
FEATURE [App::MeasureDistance] Distance002  label="Distance: 1.67 mm"
  Distance = 1.66921
  P1 = (99.2361,4.7524,71.7)
  P2 = (99.2347,6.42161,71.7)
FEATURE [Sketcher::SketchObject] Sketch018
  FullyConstrained = true
  sketch-geometry (7):
    g0: LineSegment StartX=0 StartY=0 StartZ=0 EndX=0 EndY=6 EndZ=0
    g1: Circle CenterX=0 CenterY=0 CenterZ=0 NormalX=0 NormalY=0 NormalZ=1 AngleXU=0 Radius=1
    g2: Circle CenterX=8 CenterY=6 CenterZ=0 NormalX=0 NormalY=0 NormalZ=1 AngleXU=0 Radius=1
    g3: BSplineCurve PolesCount=3 KnotsCount=2 Degree=2 IsPeriodic=0
    g4: GeomPoint X=0 Y=0 Z=0
    g5: GeomPoint X=8 Y=6 Z=0
    g6: LineSegment StartX=0 StartY=6 StartZ=0 EndX=8 EndY=6 EndZ=0
  constraints (14):
    c: Coincident(g0,g-1)
    c: Distance(g0) = 6
    c: Vertical(g0)
    c: Coincident(g3,g0)
    c: Weight(g1) = 1
    c: Equal(g1,g2)
    c: InternalAlignment(g1,g3)
    c: InternalAlignment(g2,g3)
    c: InternalAlignment(g4,g3)
    c: InternalAlignment(g5,g3)
    c: Block(g3)
    c: Coincident(g6,g0)
    c: Coincident(g6,g3)
    c: Horizontal(g6)
FEATURE [Part::Extrusion] Extrude012  label="caseScrewPillarBracket"
  Base = -> Sketch018
  Dir = (0,0,1)
  DirMode = 2
  FaceMakerClass = Part::FaceMakerBullseye
  LengthFwd = 2.4
  LengthRev = 0
  Placement = pos=(15.76,29,8.8) rot=(0,1,0;0rad)
  Solid = true
  Symmetric = false
FEATURE [Sketcher::SketchObject] Sketch019
  FullyConstrained = true
  sketch-geometry (7):
    g0: LineSegment StartX=0 StartY=0 StartZ=0 EndX=0 EndY=6 EndZ=0
    g1: Circle CenterX=0 CenterY=0 CenterZ=0 NormalX=0 NormalY=0 NormalZ=1 AngleXU=0 Radius=1
    g2: Circle CenterX=8 CenterY=6 CenterZ=0 NormalX=0 NormalY=0 NormalZ=1 AngleXU=0 Radius=1
    g3: BSplineCurve PolesCount=3 KnotsCount=2 Degree=2 IsPeriodic=0
    g4: GeomPoint X=0 Y=0 Z=0
    g5: GeomPoint X=8 Y=6 Z=0
    g6: LineSegment StartX=0 StartY=6 StartZ=0 EndX=8 EndY=6 EndZ=0
  constraints (14):
    c: Coincident(g0,g-1)
    c: Distance(g0) = 6
    c: Vertical(g0)
    c: Coincident(g3,g0)
    c: Weight(g1) = 1
    c: Equal(g1,g2)
    c: InternalAlignment(g1,g3)
    c: InternalAlignment(g2,g3)
    c: InternalAlignment(g4,g3)
    c: InternalAlignment(g5,g3)
    c: Block(g3)
    c: Coincident(g6,g0)
    c: Coincident(g6,g3)
    c: Horizontal(g6)
FEATURE [Part::Extrusion] Extrude013  label="caseScrewPillarBracket001"
  Base = -> Sketch019
  Dir = (0,0,1)
  DirMode = 2
  FaceMakerClass = Part::FaceMakerBullseye
  LengthFwd = 2.4
  LengthRev = 0
  Placement = pos=(15.76,29,60.8) rot=(0,0,1;0rad)
  Solid = true
  Symmetric = false
FEATURE [Sketcher::SketchObject] Sketch020
  FullyConstrained = true
  sketch-geometry (7):
    g0: LineSegment StartX=0 StartY=0 StartZ=0 EndX=0 EndY=6 EndZ=0
    g1: Circle CenterX=0 CenterY=0 CenterZ=0 NormalX=0 NormalY=0 NormalZ=1 AngleXU=0 Radius=1
    g2: Circle CenterX=8 CenterY=6 CenterZ=0 NormalX=0 NormalY=0 NormalZ=1 AngleXU=0 Radius=1
    g3: BSplineCurve PolesCount=3 KnotsCount=2 Degree=2 IsPeriodic=0
    g4: GeomPoint X=0 Y=0 Z=0
    g5: GeomPoint X=8 Y=6 Z=0
    g6: LineSegment StartX=0 StartY=6 StartZ=0 EndX=8 EndY=6 EndZ=0
  constraints (14):
    c: Coincident(g0,g-1)
    c: Distance(g0) = 6
    c: Vertical(g0)
    c: Coincident(g3,g0)
    c: Weight(g1) = 1
    c: Equal(g1,g2)
    c: InternalAlignment(g1,g3)
    c: InternalAlignment(g2,g3)
    c: InternalAlignment(g4,g3)
    c: InternalAlignment(g5,g3)
    c: Block(g3)
    c: Coincident(g6,g0)
    c: Coincident(g6,g3)
    c: Horizontal(g6)
FEATURE [Part::Extrusion] Extrude014  label="caseScrewPillarBracket002"
  Base = -> Sketch020
  Dir = (0,0,1)
  DirMode = 2
  FaceMakerClass = Part::FaceMakerBullseye
  LengthFwd = 2.4
  LengthRev = 0
  Placement = pos=(13.7,29,13.26) rot=(0,1,0;-1.5708rad)
  Solid = true
  Symmetric = false
FEATURE [Sketcher::SketchObject] Sketch021
  FullyConstrained = true
  sketch-geometry (7):
    g0: LineSegment StartX=0 StartY=0 StartZ=0 EndX=0 EndY=6 EndZ=0
    g1: Circle CenterX=0 CenterY=0 CenterZ=0 NormalX=0 NormalY=0 NormalZ=1 AngleXU=0 Radius=1
    g2: Circle CenterX=8 CenterY=6 CenterZ=0 NormalX=0 NormalY=0 NormalZ=1 AngleXU=0 Radius=1
    g3: BSplineCurve PolesCount=3 KnotsCount=2 Degree=2 IsPeriodic=0
    g4: GeomPoint X=0 Y=0 Z=0
    g5: GeomPoint X=8 Y=6 Z=0
    g6: LineSegment StartX=0 StartY=6 StartZ=0 EndX=8 EndY=6 EndZ=0
  constraints (14):
    c: Coincident(g0,g-1)
    c: Distance(g0) = 6
    c: Vertical(g0)
    c: Coincident(g3,g0)
    c: Weight(g1) = 1
    c: Equal(g1,g2)
    c: InternalAlignment(g1,g3)
    c: InternalAlignment(g2,g3)
    c: InternalAlignment(g4,g3)
    c: InternalAlignment(g5,g3)
    c: Block(g3)
    c: Coincident(g6,g0)
    c: Coincident(g6,g3)
    c: Horizontal(g6)
FEATURE [Part::Extrusion] Extrude015  label="caseScrewPillarBracket003"
  Base = -> Sketch021
  Dir = (0,0,1)
  DirMode = 2
  FaceMakerClass = Part::FaceMakerBullseye
  LengthFwd = 2.4
  LengthRev = 0
  Placement = pos=(11.3,29,58.74) rot=(0,1,0;1.5708rad)
  Solid = true
  Symmetric = false
FEATURE [Sketcher::SketchObject] Sketch022
  FullyConstrained = true
  sketch-geometry (7):
    g0: LineSegment StartX=0 StartY=0 StartZ=0 EndX=0 EndY=6 EndZ=0
    g1: Circle CenterX=0 CenterY=0 CenterZ=0 NormalX=0 NormalY=0 NormalZ=1 AngleXU=0 Radius=1
    g2: Circle CenterX=8 CenterY=6 CenterZ=0 NormalX=0 NormalY=0 NormalZ=1 AngleXU=0 Radius=1
    g3: BSplineCurve PolesCount=3 KnotsCount=2 Degree=2 IsPeriodic=0
    g4: GeomPoint X=0 Y=0 Z=0
    g5: GeomPoint X=8 Y=6 Z=0
    g6: LineSegment StartX=0 StartY=6 StartZ=0 EndX=8 EndY=6 EndZ=0
  constraints (14):
    c: Coincident(g0,g-1)
    c: Distance(g0) = 6
    c: Vertical(g0)
    c: Coincident(g3,g0)
    c: Weight(g1) = 1
    c: Equal(g1,g2)
    c: InternalAlignment(g1,g3)
    c: InternalAlignment(g2,g3)
    c: InternalAlignment(g4,g3)
    c: InternalAlignment(g5,g3)
    c: Block(g3)
    c: Coincident(g6,g0)
    c: Coincident(g6,g3)
    c: Horizontal(g6)
FEATURE [Part::Extrusion] Extrude016  label="caseScrewPillarBracket004"
  Base = -> Sketch022
  Dir = (0,0,1)
  DirMode = 2
  FaceMakerClass = Part::FaceMakerBullseye
  LengthFwd = 2.4
  LengthRev = 0
  Placement = pos=(88.3,29,65.23) rot=(0,1,0;1.5708rad)
  Solid = true
  Symmetric = false
FEATURE [Sketcher::SketchObject] Sketch023
  FullyConstrained = true
  sketch-geometry (7):
    g0: LineSegment StartX=0 StartY=0 StartZ=0 EndX=0 EndY=6 EndZ=0
    g1: Circle CenterX=0 CenterY=0 CenterZ=0 NormalX=0 NormalY=0 NormalZ=1 AngleXU=0 Radius=1
    g2: Circle CenterX=8 CenterY=6 CenterZ=0 NormalX=0 NormalY=0 NormalZ=1 AngleXU=0 Radius=1
    g3: BSplineCurve PolesCount=3 KnotsCount=2 Degree=2 IsPeriodic=0
    g4: GeomPoint X=0 Y=0 Z=0
    g5: GeomPoint X=8 Y=6 Z=0
    g6: LineSegment StartX=0 StartY=6 StartZ=0 EndX=8 EndY=6 EndZ=0
  constraints (14):
    c: Coincident(g0,g-1)
    c: Distance(g0) = 6
    c: Vertical(g0)
    c: Coincident(g3,g0)
    c: Weight(g1) = 1
    c: Equal(g1,g2)
    c: InternalAlignment(g1,g3)
    c: InternalAlignment(g2,g3)
    c: InternalAlignment(g4,g3)
    c: InternalAlignment(g5,g3)
    c: Block(g3)
    c: Coincident(g6,g0)
    c: Coincident(g6,g3)
    c: Horizontal(g6)
FEATURE [Part::Extrusion] Extrude017  label="caseScrewPillarBracket005"
  Base = -> Sketch023
  Dir = (0,0,1)
  DirMode = 2
  FaceMakerClass = Part::FaceMakerBullseye
  LengthFwd = 2.4
  LengthRev = 0
  Placement = pos=(90.7,29,6.77) rot=(0,-1,0;1.5708rad)
  Solid = true
  Symmetric = false
FEATURE [Sketcher::SketchObject] Sketch024
  FullyConstrained = true
  sketch-geometry (7):
    g0: LineSegment StartX=0 StartY=0 StartZ=0 EndX=0 EndY=6 EndZ=0
    g1: Circle CenterX=0 CenterY=0 CenterZ=0 NormalX=0 NormalY=0 NormalZ=1 AngleXU=0 Radius=1
    g2: Circle CenterX=8 CenterY=6 CenterZ=0 NormalX=0 NormalY=0 NormalZ=1 AngleXU=0 Radius=1
    g3: BSplineCurve PolesCount=3 KnotsCount=2 Degree=2 IsPeriodic=0
    g4: GeomPoint X=0 Y=0 Z=0
    g5: GeomPoint X=8 Y=6 Z=0
    g6: LineSegment StartX=0 StartY=6 StartZ=0 EndX=8 EndY=6 EndZ=0
  constraints (14):
    c: Coincident(g0,g-1)
    c: Distance(g0) = 6
    c: Vertical(g0)
    c: Coincident(g3,g0)
    c: Weight(g1) = 1
    c: Equal(g1,g2)
    c: InternalAlignment(g1,g3)
    c: InternalAlignment(g2,g3)
    c: InternalAlignment(g4,g3)
    c: InternalAlignment(g5,g3)
    c: Block(g3)
    c: Coincident(g6,g0)
    c: Coincident(g6,g3)
    c: Horizontal(g6)
FEATURE [Part::Extrusion] Extrude018  label="caseScrewPillarBracket006"
  Base = -> Sketch024
  Dir = (0,0,1)
  DirMode = 2
  FaceMakerClass = Part::FaceMakerBullseye
  LengthFwd = 2.4
  LengthRev = 0
  Placement = pos=(103.7,29,6.77) rot=(0,-1,0;1.5708rad)
  Solid = true
  Symmetric = false
FEATURE [Sketcher::SketchObject] Sketch025
  FullyConstrained = true
  sketch-geometry (7):
    g0: LineSegment StartX=0 StartY=0 StartZ=0 EndX=0 EndY=6 EndZ=0
    g1: Circle CenterX=0 CenterY=0 CenterZ=0 NormalX=0 NormalY=0 NormalZ=1 AngleXU=0 Radius=1
    g2: Circle CenterX=8 CenterY=6 CenterZ=0 NormalX=0 NormalY=0 NormalZ=1 AngleXU=0 Radius=1
    g3: BSplineCurve PolesCount=3 KnotsCount=2 Degree=2 IsPeriodic=0
    g4: GeomPoint X=0 Y=0 Z=0
    g5: GeomPoint X=8 Y=6 Z=0
    g6: LineSegment StartX=0 StartY=6 StartZ=0 EndX=8 EndY=6 EndZ=0
  constraints (14):
    c: Coincident(g0,g-1)
    c: Distance(g0) = 6
    c: Vertical(g0)
    c: Coincident(g3,g0)
    c: Weight(g1) = 1
    c: Equal(g1,g2)
    c: InternalAlignment(g1,g3)
    c: InternalAlignment(g2,g3)
    c: InternalAlignment(g4,g3)
    c: InternalAlignment(g5,g3)
    c: Block(g3)
    c: Coincident(g6,g0)
    c: Coincident(g6,g3)
    c: Horizontal(g6)
FEATURE [Part::Extrusion] Extrude019  label="caseScrewPillarBracket007"
  Base = -> Sketch025
  Dir = (0,0,1)
  DirMode = 2
  FaceMakerClass = Part::FaceMakerBullseye
  LengthFwd = 2.4
  LengthRev = 0
  Placement = pos=(101.3,29,65.23) rot=(0,1,0;1.5708rad)
  Solid = true
  Symmetric = false
FEATURE [Part::Box] Box011  label="frontCaseScrewPillarBracket"
  AttacherType = Attacher::AttachEngine3D
  Height = 2.4
  Length = 16
  Placement = pos=(87,28,2.3) rot=(0,0,1;0rad)
  Width = 7
FEATURE [Part::Box] Box012  label="frontCaseScrewPillarBracket001"
  AttacherType = Attacher::AttachEngine3D
  Height = 2.4
  Length = 16
  Placement = pos=(87,28,67.3) rot=(0,0,1;0rad)
  Width = 7
FEATURE [Sketcher::SketchObject] Sketch026
  FullyConstrained = true
  sketch-geometry (17):
    g0: Circle CenterX=-3.5 CenterY=23.5 CenterZ=0 NormalX=0 NormalY=0 NormalZ=1 AngleXU=0 Radius=1
    g1: Circle CenterX=-1 CenterY=15.25 CenterZ=0 NormalX=0 NormalY=0 NormalZ=1 AngleXU=0 Radius=1
    g2: Circle CenterX=-3.5 CenterY=7 CenterZ=0 NormalX=0 NormalY=0 NormalZ=1 AngleXU=0 Radius=1
    g3: BSplineCurve PolesCount=3 KnotsCount=2 Degree=2 IsPeriodic=0
    g4: GeomPoint X=-3.5 Y=23.5 Z=0
    g5: GeomPoint X=-3.5 Y=7 Z=0
    g6: Circle CenterX=-4.8 CenterY=30.5 CenterZ=0 NormalX=0 NormalY=0 NormalZ=1 AngleXU=0 Radius=1
    g7: Circle CenterX=-3.5 CenterY=30.5 CenterZ=0 NormalX=0 NormalY=0 NormalZ=1 AngleXU=0 Radius=1
    g8: Circle CenterX=-3.5 CenterY=29.2 CenterZ=0 NormalX=0 NormalY=0 NormalZ=1 AngleXU=0 Radius=1
    g9: BSplineCurve PolesCount=3 KnotsCount=2 Degree=2 IsPeriodic=0
    g10: GeomPoint X=-4.8 Y=30.5 Z=0
    g11: GeomPoint X=-3.5 Y=29.2 Z=0
    g12: LineSegment StartX=-3.5 StartY=29.2 StartZ=0 EndX=-3.5 EndY=23.5 EndZ=0
    g13: LineSegment StartX=-4.8 StartY=30.5 StartZ=0 EndX=0 EndY=30.5 EndZ=0
    g14: LineSegment StartX=-3.5 StartY=5 StartZ=0 EndX=-3.5 EndY=7 EndZ=0
    g15: LineSegment StartX=0 StartY=5 StartZ=0 EndX=0 EndY=30.5 EndZ=0
    g16: LineSegment StartX=-3.5 StartY=5 StartZ=0 EndX=0 EndY=5 EndZ=0
  constraints (33):
    c: Weight(g0) = 1
    c: Equal(g0,g1)
    c: Equal(g0,g2)
    c: InternalAlignment(g0,g3)
    c: InternalAlignment(g1,g3)
    c: InternalAlignment(g2,g3)
    c: InternalAlignment(g4,g3)
    c: InternalAlignment(g5,g3)
    c: Block(g3)
    c: Weight(g6) = 1
    c: Equal(g6,g7)
    c: Equal(g6,g8)
    c: InternalAlignment(g6,g9)
    c: InternalAlignment(g7,g9)
    c: InternalAlignment(g8,g9)
    c: InternalAlignment(g10,g9)
    c: InternalAlignment(g11,g9)
    c: Block(g9)
    c: Coincident(g12,g9)
    c: Coincident(g12,g3)
    c: Vertical(g12)
    c: Coincident(g13,g9)
    c: Horizontal(g13)
    c: Distance(g13) = 4.8
    c: Coincident(g14,g3)
    c: Vertical(g14)
    c: Coincident(g15,g13)
    c: Vertical(g15)
    c: Tangent(g15,g1)
    c: Distance(g14) = 2
    c: Coincident(g16,g14)
    c: Horizontal(g16)
    c: Coincident(g15,g16)
FEATURE [Part::Feature] Face050
  shape: bbox 4.8 x 25.5 x 2e-07 mm, 1 faces, 0 solids (baked)
FEATURE [Part::Revolution] Revolve054  label="moreFrontCaseScrewPost001"
  Angle = 360
  Axis = (0,1,0)
  Base = (0,0,0)
  FaceMakerClass = Part::FaceMakerBullseye
  Placement = pos=(102.5,4.5,3.5) rot=(0,0,1;0rad)
  Solid = false
  Source = -> Face050
  Symmetric = false
FEATURE [Part::Feature] Face051
  shape: bbox 4.8 x 25.5 x 2e-07 mm, 1 faces, 0 solids (baked)
FEATURE [Part::Revolution] Revolve055  label="moreFrontCaseScrewPost002"
  Angle = 360
  Axis = (0,1,0)
  Base = (0,0,0)
  FaceMakerClass = Part::FaceMakerBullseye
  Placement = pos=(102.5,4.5,68.5) rot=(0,0,1;0rad)
  Solid = false
  Source = -> Face051
  Symmetric = false
FEATURE [Sketcher::SketchObject] Sketch027
  FullyConstrained = true
  sketch-geometry (10):
    g0: LineSegment StartX=-1.6 StartY=4.7 StartZ=0 EndX=-1.6 EndY=1.7 EndZ=0
    g1: LineSegment StartX=-3.5 StartY=4.7 StartZ=0 EndX=-1.6 EndY=4.7 EndZ=0
    g2: LineSegment StartX=-1.6 StartY=1.7 StartZ=0 EndX=-1.6 EndY=1.5 EndZ=0
    g3: LineSegment StartX=-1.6 StartY=1.5 StartZ=0 EndX=-5.2 EndY=1.5 EndZ=0
    g4: Circle CenterX=-3.5 CenterY=4.7 CenterZ=0 NormalX=0 NormalY=0 NormalZ=1 AngleXU=0 Radius=1
    g5: Circle CenterX=-3.59627 CenterY=2.99743 CenterZ=0 NormalX=0 NormalY=0 NormalZ=1 AngleXU=0 Radius=1
    g6: Circle CenterX=-5.2 CenterY=1.5 CenterZ=0 NormalX=0 NormalY=0 NormalZ=1 AngleXU=0 Radius=1
    g7: BSplineCurve PolesCount=3 KnotsCount=2 Degree=2 IsPeriodic=0
    g8: GeomPoint X=-3.5 Y=4.7 Z=0
    g9: GeomPoint X=-5.2 Y=1.5 Z=0
  constraints (23):
    c: Vertical(g0)
    c: Distance(g0) = 3
    c: Coincident(g1,g0)
    c: Horizontal(g1)
    c: Block(g0)
    c: Block(g1)
    c: Coincident(g2,g0)
    c: Vertical(g2)
    c: Distance(g2) = 0.2
    c: Coincident(g3,g2)
    c: Horizontal(g3)
    c: Block(g3)
    c: Coincident(g7,g1)
    c: Weight(g4) = 1
    c: Equal(g4,g5)
    c: Equal(g4,g6)
    c: Coincident(g7,g3)
    c: InternalAlignment(g4,g7)
    c: InternalAlignment(g5,g7)
    c: InternalAlignment(g6,g7)
    c: InternalAlignment(g8,g7)
    c: InternalAlignment(g9,g7)
    c: Block(g7)
FEATURE [Sketcher::SketchObject] Sketch028
  FullyConstrained = true
  sketch-geometry (18):
    g0: LineSegment StartX=0 StartY=3e-16 StartZ=0 EndX=0 EndY=1.7 EndZ=0
    g1: LineSegment StartX=-3.5 StartY=0 StartZ=0 EndX=-3.5 EndY=0.9 EndZ=0
    g2: Circle CenterX=-2.7 CenterY=1.7 CenterZ=0 NormalX=0 NormalY=0 NormalZ=1 AngleXU=0 Radius=1
    g3: Circle CenterX=-3.5 CenterY=1.7 CenterZ=0 NormalX=0 NormalY=0 NormalZ=1 AngleXU=0 Radius=1
    g4: Circle CenterX=-3.5 CenterY=0.9 CenterZ=0 NormalX=0 NormalY=0 NormalZ=1 AngleXU=0 Radius=1
    g5: BSplineCurve PolesCount=3 KnotsCount=2 Degree=2 IsPeriodic=0
    g6: GeomPoint X=-2.7 Y=1.7 Z=0
    g7: GeomPoint X=-3.5 Y=0.9 Z=0
    g8: LineSegment StartX=-3.5 StartY=0 StartZ=0 EndX=-3.5 EndY=-7 EndZ=0
    g9: LineSegment StartX=0 StartY=3e-16 StartZ=0 EndX=0 EndY=-7 EndZ=0
    g10: LineSegment StartX=-3.5 StartY=-7 StartZ=0 EndX=0 EndY=-7 EndZ=0
    g11: LineSegment StartX=-2.7 StartY=1.7 StartZ=0 EndX=-1.6 EndY=1.7 EndZ=0
    g12: LineSegment StartX=0 StartY=1.7 StartZ=0 EndX=0 EndY=4.5 EndZ=0
    g13: LineSegment StartX=0 StartY=4.5 StartZ=0 EndX=0 EndY=10.8 EndZ=0
    g14: LineSegment StartX=0 StartY=10.8 StartZ=0 EndX=-2 EndY=10.8 EndZ=0
    g15: LineSegment StartX=-1.6 StartY=4.7 StartZ=0 EndX=-1.6 EndY=1.7 EndZ=0
    g16: LineSegment StartX=-1.6 StartY=4.7 StartZ=0 EndX=-2 EndY=4.7 EndZ=0
    g17: LineSegment StartX=-2 StartY=4.7 StartZ=0 EndX=-2 EndY=10.8 EndZ=0
  constraints (44):
    c: Vertical(g0)
    c: Vertical(g1)
    c: Distance(g1) = 0.9
    c: Block(g0)
    c: Distance(g0) = 1.7
    c: Weight(g2) = 1
    c: Equal(g2,g3)
    c: Equal(g2,g4)
    c: Coincident(g5,g1)
    c: InternalAlignment(g2,g5)
    c: InternalAlignment(g3,g5)
    c: InternalAlignment(g4,g5)
    c: InternalAlignment(g6,g5)
    c: InternalAlignment(g7,g5)
    c: Block(g5)
    c: Coincident(g8,g1)
    c: Vertical(g8)
    c: Distance(g8) = 7
    c: Vertical(g9)
    c: Equal(g8,g9) = 7
    c: Coincident(g9,g0)
    c: Coincident(g10,g8)
    c: Coincident(g10,g9)
    c: Horizontal(g10)
    c: Coincident(g11,g5)
    c: Horizontal(g11)
    c: Coincident(g12,g0)
    c: Vertical(g12)
    c: Distance(g12) = 2.8
    c: Coincident(g13,g12)
    c: Vertical(g13)
    c: Distance(g13) = 6.3
    c: Coincident(g14,g13)
    c: Horizontal(g14)
    c: Distance(g14) = 2
    c: Vertical(g15)
    c: Distance(g15) = 3
    c: Block(g11)
    c: Coincident(g15,g11)
    c: Coincident(g16,g15)
    c: Horizontal(g16)
    c: Coincident(g17,g16)
    c: Coincident(g17,g14)
    c: Vertical(g17)
FEATURE [Part::Revolution] Revolve040  label="backCaseScrewRetainer001"
  Angle = 360
  Axis = (0,1,0)
  Base = (0,0,0)
  FaceMakerClass = Part::FaceMakerBullseye
  Placement = pos=(12.5,3,10) rot=(0,0,1;0rad)
  Solid = false
  Source = -> Face036
  Symmetric = false
FEATURE [Part::Feature] Face055
  shape: bbox 3.5 x 30.2 x 2e-07 mm, 1 faces, 0 solids (baked)
FEATURE [Part::Revolution] Revolve059  label="backCaseScrewPost"
  Angle = 360
  Axis = (0,1,0)
  Base = (0,0,0)
  FaceMakerClass = Part::FaceMakerBullseye
  Placement = pos=(12.5,4.5,10) rot=(0,0,1;0rad)
  Solid = false
  Source = -> Face055
  Symmetric = false
FEATURE [Part::Feature] Face056
  shape: bbox 3.5 x 30.2 x 2e-07 mm, 1 faces, 0 solids (baked)
FEATURE [Part::Revolution] Revolve060  label="backCaseScrewPost001"
  Angle = 360
  Axis = (0,1,0)
  Base = (0,0,0)
  FaceMakerClass = Part::FaceMakerBullseye
  Placement = pos=(12.5,4.5,62) rot=(0,0,1;0rad)
  Solid = false
  Source = -> Face056
  Symmetric = false
FEATURE [Part::Feature] Face057
  shape: bbox 3.5 x 17.8 x 2e-07 mm, 1 faces, 0 solids (baked)
FEATURE [Part::Revolution] Revolve061  label="removeToCreateScrewAndThreadedInsertHole"
  Angle = 360
  Axis = (0,1,0)
  Base = (0,0,0)
  FaceMakerClass = Part::FaceMakerBullseye
  Placement = pos=(12.5,0,10) rot=(0,0,1;0rad)
  Solid = false
  Source = -> Face057
  Symmetric = false
FEATURE [Part::Feature] Face058
  shape: bbox 3.5 x 17.8 x 2e-07 mm, 1 faces, 0 solids (baked)
FEATURE [Part::Revolution] Revolve062  label="removeToCreateScrewAndThreadedInsertHole001"
  Angle = 360
  Axis = (0,1,0)
  Base = (0,0,0)
  FaceMakerClass = Part::FaceMakerBullseye
  Placement = pos=(12.5,0,62) rot=(0,0,1;0rad)
  Solid = false
  Source = -> Face058
  Symmetric = false
FEATURE [Part::Feature] Face059
  shape: bbox 3.5 x 17.8 x 2e-07 mm, 1 faces, 0 solids (baked)
FEATURE [Part::Revolution] Revolve063  label="removeToCreateScrewAndThreadedInsertHole002"
  Angle = 360
  Axis = (0,1,0)
  Base = (0,0,0)
  FaceMakerClass = Part::FaceMakerBullseye
  Placement = pos=(89.5,0,68.5) rot=(0,0,1;0rad)
  Solid = false
  Source = -> Face059
  Symmetric = false
FEATURE [Part::Feature] Face060
  shape: bbox 3.5 x 17.8 x 2e-07 mm, 1 faces, 0 solids (baked)
FEATURE [Part::Revolution] Revolve064  label="removeToCreateScrewAndThreadedInsertHole003"
  Angle = 360
  Axis = (0,1,0)
  Base = (0,0,0)
  FaceMakerClass = Part::FaceMakerBullseye
  Placement = pos=(89.5,0,3.5) rot=(0,0,1;0rad)
  Solid = false
  Source = -> Face060
  Symmetric = false
FEATURE [Part::Feature] Face061
  shape: bbox 3.5 x 17.8 x 2e-07 mm, 1 faces, 0 solids (baked)
FEATURE [Part::Revolution] Revolve065  label="removeToCreateScrewAndThreadedInsertHole004"
  Angle = 360
  Axis = (0,1,0)
  Base = (0,0,0)
  FaceMakerClass = Part::FaceMakerBullseye
  Placement = pos=(102.5,4.7,3.5) rot=(0,0,1;0rad)
  Solid = false
  Source = -> Face061
  Symmetric = false
FEATURE [Part::Feature] Face062
  shape: bbox 3.5 x 17.8 x 2e-07 mm, 1 faces, 0 solids (baked)
FEATURE [Part::Revolution] Revolve066  label="removeToCreateScrewAndThreadedInsertHole005"
  Angle = 360
  Axis = (0,1,0)
  Base = (0,0,0)
  FaceMakerClass = Part::FaceMakerBullseye
  Placement = pos=(102.5,4.7,68.5) rot=(0,0,1;0rad)
  Solid = false
  Source = -> Face062
  Symmetric = false
FEATURE [Part::MultiFuse] Fusion047  label="makeHoles"
  Shapes = -> [Revolve066,Revolve065,Revolve064,Revolve063,Revolve062,Revolve061]
FEATURE [Part::Feature] Face063
  shape: bbox 3.6 x 3.2 x 2e-07 mm, 1 faces, 0 solids (baked)
FEATURE [Part::Revolution] Revolve067  label="moreFrontCaseScrewRetainer002"
  Angle = 360
  Axis = (0,1,0)
  Base = (0,0,0)
  FaceMakerClass = Part::FaceMakerBullseye
  Placement = pos=(102.5,4.5,68.5) rot=(0,0,1;0rad)
  Solid = false
  Source = -> Face063
  Symmetric = false
FEATURE [Part::Feature] Face064
  shape: bbox 3.6 x 3.2 x 2e-07 mm, 1 faces, 0 solids (baked)
FEATURE [Part::Revolution] Revolve068  label="moreFrontCaseScrewRetainer003"
  Angle = 360
  Axis = (0,1,0)
  Base = (0,0,0)
  FaceMakerClass = Part::FaceMakerBullseye
  Placement = pos=(102.5,4.5,3.5) rot=(0,0,1;0rad)
  Solid = false
  Source = -> Face064
  Symmetric = false
FEATURE [Part::Cut] Cut014  label="bottom003"
  Base = -> Cut007
  Tool = -> Fusion047
FEATURE [Part::Feature] Face065
  shape: bbox 3.5 x 17.8 x 2e-07 mm, 1 faces, 0 solids (baked)
FEATURE [Part::Revolution] Revolve069  label="removeToCreateScrewAndThreadedInsertHole006"
  Angle = 360
  Axis = (0,1,0)
  Base = (0,0,0)
  FaceMakerClass = Part::FaceMakerBullseye
  Placement = pos=(12.5,0,10) rot=(0,0,1;0rad)
  Solid = false
  Source = -> Face065
  Symmetric = false
FEATURE [Part::Feature] Face066
  shape: bbox 3.5 x 17.8 x 2e-07 mm, 1 faces, 0 solids (baked)
FEATURE [Part::Revolution] Revolve070  label="removeToCreateScrewAndThreadedInsertHole007"
  Angle = 360
  Axis = (0,1,0)
  Base = (0,0,0)
  FaceMakerClass = Part::FaceMakerBullseye
  Placement = pos=(12.5,0,62) rot=(0,0,1;0rad)
  Solid = false
  Source = -> Face066
  Symmetric = false
FEATURE [Part::Feature] Face067
  shape: bbox 3.5 x 17.8 x 2e-07 mm, 1 faces, 0 solids (baked)
FEATURE [Part::Revolution] Revolve071  label="removeToCreateScrewAndThreadedInsertHole008"
  Angle = 360
  Axis = (0,1,0)
  Base = (0,0,0)
  FaceMakerClass = Part::FaceMakerBullseye
  Placement = pos=(89.5,0,68.5) rot=(0,0,1;0rad)
  Solid = false
  Source = -> Face067
  Symmetric = false
FEATURE [Part::Feature] Face068
  shape: bbox 3.5 x 17.8 x 2e-07 mm, 1 faces, 0 solids (baked)
FEATURE [Part::Revolution] Revolve072  label="removeToCreateScrewAndThreadedInsertHole009"
  Angle = 360
  Axis = (0,1,0)
  Base = (0,0,0)
  FaceMakerClass = Part::FaceMakerBullseye
  Placement = pos=(89.5,0,3.5) rot=(0,0,1;0rad)
  Solid = false
  Source = -> Face068
  Symmetric = false
FEATURE [Part::Feature] Face069
  shape: bbox 3.5 x 17.8 x 2e-07 mm, 1 faces, 0 solids (baked)
FEATURE [Part::Feature] Face070
  shape: bbox 3.5 x 17.8 x 2e-07 mm, 1 faces, 0 solids (baked)
FEATURE [Part::Revolution] Revolve073  label="removeToCreateScrewAndThreadedInsertHole010"
  Angle = 360
  Axis = (0,1,0)
  Base = (0,0,0)
  FaceMakerClass = Part::FaceMakerBullseye
  Placement = pos=(102.5,4.7,3.5) rot=(0,0,1;0rad)
  Solid = false
  Source = -> Face069
  Symmetric = false
FEATURE [Part::Revolution] Revolve074  label="removeToCreateScrewAndThreadedInsertHole011"
  Angle = 360
  Axis = (0,1,0)
  Base = (0,0,0)
  FaceMakerClass = Part::FaceMakerBullseye
  Placement = pos=(102.5,4.7,68.5) rot=(0,0,1;0rad)
  Solid = false
  Source = -> Face070
  Symmetric = false
FEATURE [Part::MultiFuse] Fusion048  label="makeHoles001"
  Shapes = -> [Revolve074,Revolve073,Revolve072,Revolve071,Revolve070,Revolve069]
FEATURE [Part::MultiFuse] Fusion049  label="caseScrewRetainers"
  Shapes = -> [Revolve067,Revolve068,Revolve048,Revolve047,Revolve039,Revolve040]
FEATURE [Part::Cut] Cut015  label="caseScrewRetainers001"
  Base = -> Fusion049
  Tool = -> Fusion048
FEATURE [Part::MultiFuse] Fusion050  label="casePillars"
  Shapes = -> [Revolve055,Revolve054,Revolve043,Revolve046,Revolve059,Revolve060]
FEATURE [Part::Feature] Face071 .. Face076  x6 (patterned run collapsed; names and placements below)
  shape: bbox 3.5 x 17.8 x 2e-07 mm, 1 faces, 0 solids (baked)
FEATURE [Part::Revolution] Revolve075  label="removeToCreateScrewAndThreadedInsertHole012"
  Angle = 360
  Axis = (0,1,0)
  Base = (0,0,0)
  FaceMakerClass = Part::FaceMakerBullseye
  Placement = pos=(12.5,0,10) rot=(0,0,1;0rad)
  Solid = false
  Source = -> Face071
  Symmetric = false
FEATURE [Part::Revolution] Revolve076  label="removeToCreateScrewAndThreadedInsertHole013"
  Angle = 360
  Axis = (0,1,0)
  Base = (0,0,0)
  FaceMakerClass = Part::FaceMakerBullseye
  Placement = pos=(12.5,0,62) rot=(0,0,1;0rad)
  Solid = false
  Source = -> Face072
  Symmetric = false
FEATURE [Part::Revolution] Revolve077  label="removeToCreateScrewAndThreadedInsertHole014"
  Angle = 360
  Axis = (0,1,0)
  Base = (0,0,0)
  FaceMakerClass = Part::FaceMakerBullseye
  Placement = pos=(89.5,0,68.5) rot=(0,0,1;0rad)
  Solid = false
  Source = -> Face073
  Symmetric = false
FEATURE [Part::Revolution] Revolve078  label="removeToCreateScrewAndThreadedInsertHole015"
  Angle = 360
  Axis = (0,1,0)
  Base = (0,0,0)
  FaceMakerClass = Part::FaceMakerBullseye
  Placement = pos=(89.5,0,3.5) rot=(0,0,1;0rad)
  Solid = false
  Source = -> Face074
  Symmetric = false
FEATURE [Part::Revolution] Revolve079  label="removeToCreateScrewAndThreadedInsertHole016"
  Angle = 360
  Axis = (0,1,0)
  Base = (0,0,0)
  FaceMakerClass = Part::FaceMakerBullseye
  Placement = pos=(102.5,4.7,3.5) rot=(0,0,1;0rad)
  Solid = false
  Source = -> Face075
  Symmetric = false
FEATURE [Part::Revolution] Revolve080  label="removeToCreateScrewAndThreadedInsertHole017"
  Angle = 360
  Axis = (0,1,0)
  Base = (0,0,0)
  FaceMakerClass = Part::FaceMakerBullseye
  Placement = pos=(102.5,4.7,68.5) rot=(0,0,1;0rad)
  Solid = false
  Source = -> Face076
  Symmetric = false
FEATURE [Part::MultiFuse] Fusion051  label="makeHoles002"
  Shapes = -> [Revolve080,Revolve079,Revolve078,Revolve077,Revolve076,Revolve075]
FEATURE [Part::Cut] Cut016  label="caesPillars"
  Base = -> Fusion050
  Tool = -> Fusion051
FEATURE [Part::Revolution] Revolve009  label="plugHousing016"
  Angle = 360
  Axis = (0,1,0)
  Base = (0,0,0)
  FaceMakerClass = Part::FaceMakerBullseye
  Placement = pos=(0,0,36.15) rot=(0,0,1;0rad)
  Solid = false
  Source = -> Face012
  Symmetric = false
FEATURE [Part::MultiFuse] Fusion014  label="plugHousing023"
  Placement = pos=(0,0,0) rot=(0,0,1;1.5708rad)
  Shapes = -> [Revolve011,Revolve009]
FEATURE [Part::Revolution] Revolve010  label="plugHousing017"
  Angle = 360
  Axis = (0,1,0)
  Base = (0,0,0)
  FaceMakerClass = Part::FaceMakerBullseye
  Placement = pos=(0,0,36.15) rot=(0,0,1;0rad)
  Solid = false
  Source = -> Face014
  Symmetric = false
FEATURE [Part::MultiFuse] Fusion015  label="plugHousing024"
  Placement = pos=(0,0,0) rot=(0,0,1;1.5708rad)
  Shapes = -> [Revolve010,Revolve015]
FEATURE [Part::Revolution] Revolve014  label="plugHousing026"
  Angle = 360
  Axis = (0,1,0)
  Base = (0,0,0)
  FaceMakerClass = Part::FaceMakerBullseye
  Placement = pos=(0,0,36.15) rot=(0,0,1;0rad)
  Solid = false
  Source = -> Face011
  Symmetric = false
FEATURE [Part::Revolution] Revolve013  label="plugHousing025"
  Angle = 360
  Axis = (0,1,0)
  Base = (0,0,0)
  FaceMakerClass = Part::FaceMakerBullseye
  Placement = pos=(0,0,36.15) rot=(0,0,1;0rad)
  Solid = false
  Source = -> Face015
  Symmetric = false
FEATURE [Part::MultiFuse] Fusion016  label="plugHousing028"
  Placement = pos=(0,19,0) rot=(0,0,1;3.14159rad)
  Shapes = -> [Fusion014,Fusion013]
FEATURE [Part::MultiFuse] Fusion011  label="plugHousing018"
  Placement = pos=(0,0,0) rot=(0,0,1;1.5708rad)
  Shapes = -> [Revolve014,Revolve013]
FEATURE [Part::MultiFuse] Fusion012  label="plugHousing019"
  Placement = pos=(0,19,0) rot=(0,0,1;3.14159rad)
  Shapes = -> [Fusion011,Fusion015]
FEATURE [Part::MultiFuse] Fusion017  label="plugHousing029"
  Placement = pos=(122.621,0,-0.15) rot=(0,0,1;0rad)
  Shapes = -> [Fusion016,Fusion012]
FEATURE [Part::MultiFuse] Fusion052  label="casePillarRetainers"
  Shapes = -> [Extrude012,Extrude013,Extrude014,Extrude015,Extrude016,Extrude017,Extrude018,Extrude019,Box011,Box012]
FEATURE [Part::Feature] Face077
  shape: bbox 3.5 x 17.8 x 2e-07 mm, 1 faces, 0 solids (baked)
FEATURE [Part::Revolution] Revolve081  label="removeToCreateScrewAndThreadedInsertHole018"
  Angle = 360
  Axis = (0,1,0)
  Base = (0,0,0)
  FaceMakerClass = Part::FaceMakerBullseye
  Placement = pos=(62.3,30.3,19.7) rot=(0,0,1;0rad)
  Solid = false
  Source = -> Face077
  Symmetric = false
FEATURE [Part::Feature] Face078
  shape: bbox 3.5 x 17.8 x 2e-07 mm, 1 faces, 0 solids (baked)
FEATURE [Part::Revolution] Revolve082  label="removeToCreateScrewAndThreadedInsertHole019"
  Angle = 360
  Axis = (0,1,0)
  Base = (0,0,0)
  FaceMakerClass = Part::FaceMakerBullseye
  Placement = pos=(62.3,30.3,51.7) rot=(0,0,1;0rad)
  Solid = false
  Source = -> Face078
  Symmetric = false
FEATURE [Part::Feature] Face079
  shape: bbox 3.5 x 17.8 x 2e-07 mm, 1 faces, 0 solids (baked)
FEATURE [Part::Revolution] Revolve083  label="removeToCreateScrewAndThreadedInsertHole020"
  Angle = 360
  Axis = (0,1,0)
  Base = (0,0,0)
  FaceMakerClass = Part::FaceMakerBullseye
  Placement = pos=(30.3,30.3,19.7) rot=(0,0,1;0rad)
  Solid = false
  Source = -> Face079
  Symmetric = false
FEATURE [Part::Feature] Face080
  shape: bbox 3.5 x 17.8 x 2e-07 mm, 1 faces, 0 solids (baked)
FEATURE [Part::Revolution] Revolve084  label="removeToCreateScrewAndThreadedInsertHole021"
  Angle = 360
  Axis = (0,1,0)
  Base = (0,0,0)
  FaceMakerClass = Part::FaceMakerBullseye
  Placement = pos=(30.3,30.3,51.7) rot=(0,0,1;0rad)
  Solid = false
  Source = -> Face080
  Symmetric = false
FEATURE [Part::MultiFuse] Fusion053  label="createThreadedInsertHolesForFan"
  Shapes = -> [Revolve081,Revolve082,Revolve083,Revolve084]
FEATURE [Part::Cut] Cut017  label="fanScrewHousing001"
  Base = -> Fusion046
  Tool = -> Fusion053
FEATURE [Part::Feature] Face081
  shape: bbox 3.5 x 17.8 x 2e-07 mm, 1 faces, 0 solids (baked)
FEATURE [Part::Revolution] Revolve085  label="removeToCreateScrewAndThreadedInsertHole022"
  Angle = 360
  Axis = (0,1,0)
  Base = (0,0,0)
  FaceMakerClass = Part::FaceMakerBullseye
  Placement = pos=(62.3,30.3,19.7) rot=(0,0,1;0rad)
  Solid = false
  Source = -> Face081
  Symmetric = false
FEATURE [Part::Feature] Face082
  shape: bbox 3.5 x 17.8 x 2e-07 mm, 1 faces, 0 solids (baked)
FEATURE [Part::Revolution] Revolve086  label="removeToCreateScrewAndThreadedInsertHole023"
  Angle = 360
  Axis = (0,1,0)
  Base = (0,0,0)
  FaceMakerClass = Part::FaceMakerBullseye
  Placement = pos=(62.3,30.3,51.7) rot=(0,0,1;0rad)
  Solid = false
  Source = -> Face082
  Symmetric = false
FEATURE [Part::Feature] Face083
  shape: bbox 3.5 x 17.8 x 2e-07 mm, 1 faces, 0 solids (baked)
FEATURE [Part::Revolution] Revolve087  label="removeToCreateScrewAndThreadedInsertHole024"
  Angle = 360
  Axis = (0,1,0)
  Base = (0,0,0)
  FaceMakerClass = Part::FaceMakerBullseye
  Placement = pos=(30.3,30.3,19.7) rot=(0,0,1;0rad)
  Solid = false
  Source = -> Face083
  Symmetric = false
FEATURE [Part::Feature] Face084
  shape: bbox 3.5 x 17.8 x 2e-07 mm, 1 faces, 0 solids (baked)
FEATURE [Part::Revolution] Revolve088  label="removeToCreateScrewAndThreadedInsertHole025"
  Angle = 360
  Axis = (0,1,0)
  Base = (0,0,0)
  FaceMakerClass = Part::FaceMakerBullseye
  Placement = pos=(30.3,30.3,51.7) rot=(0,0,1;0rad)
  Solid = false
  Source = -> Face084
  Symmetric = false
FEATURE [Part::MultiFuse] Fusion054  label="createThreadedInsertHolesForFan001"
  Shapes = -> [Revolve085,Revolve086,Revolve087,Revolve088]
FEATURE [Part::Cut] Cut018  label="top007"
  Base = -> Fusion040
  Tool = -> Fusion054
FEATURE [Sketcher::SketchObject] Sketch029
  FullyConstrained = true
  Placement = pos=(0,0,0) rot=(-1,0,0;4.71239rad)
  sketch-geometry (39):
    g0: LineSegment StartX=0 StartY=0 StartZ=0 EndX=-38.2 EndY=0 EndZ=0
    g1: LineSegment StartX=0 StartY=0 StartZ=0 EndX=0 EndY=-38.2 EndZ=0
    g2: LineSegment StartX=0 StartY=-38.2 StartZ=0 EndX=-38.2 EndY=-38.2 EndZ=0
    g3: LineSegment StartX=-38.2 StartY=0 StartZ=0 EndX=-38.2 EndY=-38.2 EndZ=0
    g4: LineSegment StartX=-38.2 StartY=-38.2 StartZ=0 EndX=-35.7 EndY=-38.2 EndZ=0
    g5: LineSegment StartX=-38.2 StartY=0 StartZ=0 EndX=-35.7 EndY=0 EndZ=0
    g6: LineSegment StartX=0 StartY=0 StartZ=0 EndX=-2.5 EndY=0 EndZ=0
    g7: LineSegment StartX=0 StartY=-38.2 StartZ=0 EndX=-2.5 EndY=-38.2 EndZ=0
    g8: LineSegment StartX=-2.5 StartY=0 StartZ=0 EndX=-2.5 EndY=-9 EndZ=0
    g9: LineSegment StartX=-35.7 StartY=0 StartZ=0 EndX=-35.7 EndY=-9 EndZ=0
    g10: LineSegment StartX=-35.7 StartY=-38.2 StartZ=0 EndX=-35.7 EndY=-29.2 EndZ=0
    g11: LineSegment StartX=-2.5 StartY=-38.2 StartZ=0 EndX=-2.5 EndY=-29.2 EndZ=0
    g12: LineSegment StartX=-2.5 StartY=-29.2 StartZ=0 EndX=-5.5 EndY=-29.2 EndZ=0
    g13: LineSegment StartX=-35.7 StartY=-29.2 StartZ=0 EndX=-32.89 EndY=-29.2 EndZ=0
    g14: LineSegment StartX=-32.89 StartY=-29.2 StartZ=0 EndX=-32.89 EndY=-27.7 EndZ=0
    g15: LineSegment StartX=-5.5 StartY=-29.2 StartZ=0 EndX=-5.5 EndY=-27.7 EndZ=0
    g16: LineSegment StartX=-32.89 StartY=-27.7 StartZ=0 EndX=-34.39 EndY=-27.7 EndZ=0
    g17: LineSegment StartX=-5.5 StartY=-10.5 StartZ=0 EndX=-4 EndY=-10.5 EndZ=0
    g18: LineSegment StartX=-5.5 StartY=-27.7 StartZ=0 EndX=-4 EndY=-27.7 EndZ=0
    g19: LineSegment StartX=-4 StartY=-10.5 StartZ=0 EndX=-2.5 EndY=-10.5 EndZ=0
    g20: LineSegment StartX=-4 StartY=-27.7 StartZ=0 EndX=-2.5 EndY=-27.7 EndZ=0
    g21: LineSegment StartX=-34.39 StartY=-27.7 StartZ=0 EndX=-35.89 EndY=-27.7 EndZ=0
    g22: ArcOfCircle CenterX=-4 CenterY=-10.5 CenterZ=0 NormalX=0 NormalY=0 NormalZ=1 AngleXU=0 Radius=1.5 StartAngle=0 EndAngle=3.14159
    g23: ArcOfCircle CenterX=-34.39 CenterY=-27.7 CenterZ=0 NormalX=0 NormalY=0 NormalZ=1 AngleXU=0 Radius=1.5 StartAngle=3.14159 EndAngle=6.28319
    g24: ArcOfCircle CenterX=-4 CenterY=-27.7 CenterZ=0 NormalX=0 NormalY=0 NormalZ=1 AngleXU=0 Radius=1.5 StartAngle=3.14159 EndAngle=6.28319
    g25: LineSegment StartX=-35.7 StartY=-9 StartZ=0 EndX=-35.7 EndY=-10.5 EndZ=0
    g26: LineSegment StartX=-32.7 StartY=-10.5 StartZ=0 EndX=-34.2 EndY=-10.5 EndZ=0
    g27: ArcOfCircle CenterX=-34.2 CenterY=-10.5 CenterZ=0 NormalX=0 NormalY=0 NormalZ=1 AngleXU=0 Radius=1.5 StartAngle=0 EndAngle=3.14159
    g28: LineSegment StartX=-2.5 StartY=-9 StartZ=0 EndX=-2.5 EndY=-10.5 EndZ=0
    g29: LineSegment StartX=-34.2 StartY=-10.5 StartZ=0 EndX=-35.7 EndY=-10.5 EndZ=0
    g30: LineSegment StartX=-32.7 StartY=-10.5 StartZ=0 EndX=-29.7 EndY=-10.5 EndZ=0
    g31: LineSegment StartX=-29.7 StartY=-10.5 StartZ=0 EndX=-26.7 EndY=-10.5 EndZ=0
    g32: LineSegment StartX=-26.7 StartY=-10.5 StartZ=0 EndX=-23.6 EndY=-10.5 EndZ=0
    g33: LineSegment StartX=-23.6 StartY=-10.5 StartZ=0 EndX=-20.6 EndY=-10.5 EndZ=0
    g34: LineSegment StartX=-20.6 StartY=-10.5 StartZ=0 EndX=-17.6 EndY=-10.5 EndZ=0
    g35: LineSegment StartX=-17.6 StartY=-10.5 StartZ=0 EndX=-14.6 EndY=-10.5 EndZ=0
    g36: LineSegment StartX=-14.6 StartY=-10.5 StartZ=0 EndX=-11.5 EndY=-10.5 EndZ=0
    g37: LineSegment StartX=-11.5 StartY=-10.5 StartZ=0 EndX=-8.5 EndY=-10.5 EndZ=0
    g38: LineSegment StartX=-8.5 StartY=-10.5 StartZ=0 EndX=-5.5 EndY=-10.5 EndZ=0
  constraints (113):
    c: Coincident(g0,g-1)
    c: Horizontal(g0)
    c: Distance(g0) = 38.2
    c: Coincident(g1,g0)
    c: Vertical(g1)
    c: Distance(g1) = 38.2
    c: Horizontal(g2)
    c: Equal(g0,g2) = 38.2
    c: Coincident(g2,g1)
    c: Vertical(g3)
    c: Equal(g1,g3) = 38.2
    c: Coincident(g3,g0)
    c: Horizontal(g4)
    c: Coincident(g4,g2)
    c: Horizontal(g5)
    c: Coincident(g5,g0)
    c: Horizontal(g6)
    c: Coincident(g6,g0)
    c: Horizontal(g7)
    c: Coincident(g7,g1)
    c: Coincident(g8,g6)
    c: Vertical(g8)
    c: Distance(g8) = 9
    c: Vertical(g9)
    c: Equal(g8,g9) = 9
    c: Coincident(g9,g5)
    c: Coincident(g10,g4)
    c: Vertical(g10)
    c: Distance(g10) = 9
    c: Vertical(g11)
    c: Equal(g10,g11) = 9
    c: Coincident(g11,g7)
    c: Block(g0)
    c: Block(g8)
    c: Block(g9)
    c: Block(g11)
    c: Block(g10)
    c: Horizontal(g12)
    c: Coincident(g12,g11)
    c: Horizontal(g13)
    c: Coincident(g13,g10)
    c: Coincident(g14,g13)
    c: Vertical(g14)
    c: Distance(g14) = 1.5
    c: Coincident(g15,g12)
    c: Vertical(g15)
    c: Distance(g15) = 1.5
    c: Horizontal(g16)
    c: Coincident(g16,g14)
    c: Horizontal(g17)
    c: Distance(g17) = 1.5
    c: Horizontal(g18)
    c: Equal(g17,g18) = 1.5
    c: Coincident(g18,g15)
    c: Horizontal(g19)
    c: Equal(g17,g19) = 1.5
    c: Coincident(g19,g17)
    c: Horizontal(g20)
    c: Coincident(g20,g18)
    c: Horizontal(g21)
    c: Coincident(g21,g16)
    c: Coincident(g22,g17)
    c: Coincident(g22,g19)
    c: Coincident(g23,g16)
    c: Coincident(g23,g14)
    c: Coincident(g23,g21)
    c: Coincident(g24,g18)
    c: Coincident(g24,g20)
    c: Coincident(g24,g15)
    c: Block(g22)
    c: Block(g23)
    c: Block(g24)
    c: Coincident(g25,g9)
    c: Vertical(g25)
    c: Distance(g25) = 1.5
    c: Horizontal(g26)
    c: Coincident(g27,g26)
    c: Block(g27)
    c: Coincident(g28,g8)
    c: Coincident(g28,g19)
    c: Vertical(g28)
    c: Distance(g26) = 1.5
    c: Horizontal(g29)
    c: Equal(g26,g29) = 1.5
    c: Coincident(g29,g26)
    c: Horizontal(g30)
    c: Coincident(g30,g26)
    c: Horizontal(g31)
    c: Coincident(g31,g30)
    c: Horizontal(g32)
    c: Distance(g32) = 3.1
    c: Coincident(g32,g31)
    c: Horizontal(g33)
    c: Coincident(g33,g32)
    c: Horizontal(g34)
    c: Coincident(g34,g33)
    c: Horizontal(g35)
    c: Coincident(g35,g34)
    c: Horizontal(g36)
    c: Coincident(g36,g35)
    c: Horizontal(g37)
    c: Coincident(g37,g36)
    c: Distance(g36) = 3.1
    c: Coincident(g38,g37)
    c: Coincident(g38,g17)
    c: Horizontal(g38)
    c: Distance(g38) = 3
    c: Distance(g30) = 3
    c: Distance(g31) = 3
    c: Distance(g33) = 3
    c: Distance(g34) = 3
    c: Distance(g35) = 3
    c: Distance(g37) = 3
